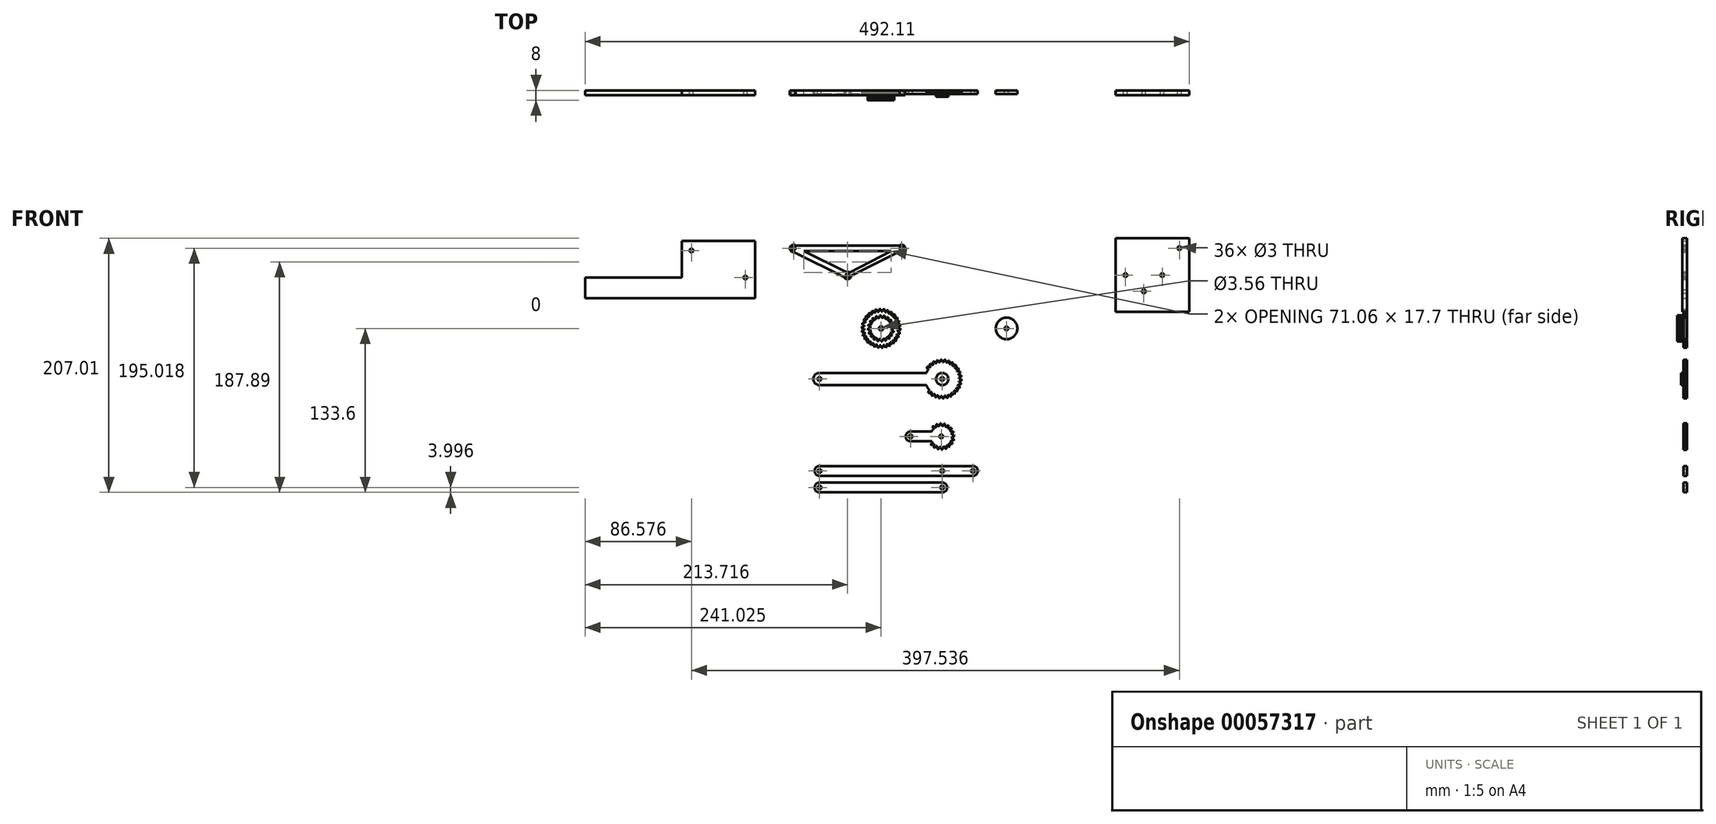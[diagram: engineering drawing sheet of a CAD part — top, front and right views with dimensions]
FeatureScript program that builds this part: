
annotation { "Feature Type Name" : "Feature", "Feature Type Description" : "" }
export const myFeature = defineFeature(function(context is Context, id is Id, definition is map)
    precondition{}
    {
        {
            var Q0;
            Q0=qCreatedBy(makeId("Front.planeOp"),FACE);
            var sketch = newSketch(context, id + "F0", { "sketchPlane" : qUnion([Q0])});
            skCircle(sketch, "E0", {"center": v(0, 0) * mm, "radius": 13.8 * mm});
            skCircle(sketch, "E1", {"center": v(0, 0) * mm, "radius": 15 * mm, "construction": true});
            skCircle(sketch, "E2", {"center": v(0, 0) * mm, "radius": 15.75 * mm, "construction": true});
            skLineSegment(sketch, "E3", {"start": v(0, 0) * mm, "end": v(0, 26.9) * mm, "construction": true});
            skCircle(sketch, "E4", {"center": v(0, 0) * mm, "radius": 14.1 * mm, "construction": true});
            skLineSegment(sketch, "E5", {"start": v(0, 0) * mm, "end": v(-1.5, 26.52) * mm, "construction": true});
            skLineSegment(sketch, "E6", {"start": v(0, 15) * mm, "end": v(-9, 15) * mm, "construction": true});
            skLineSegment(sketch, "E7", {"start": v(0, 15) * mm, "end": v(-16.93, 8.84) * mm, "construction": true});
            skCircle(sketch, "E8", {"center": v(0, 15) * mm, "radius": 2.5 * mm, "construction": true});
            skCircle(sketch, "E9", {"center": v(-2.25, 13.91) * mm, "radius": 2.5 * mm, "construction": true});
            skArc(sketch, "E10", {"start": v(-0.54, 15.74) * mm, "mid": v(0.06, 14.86) * mm, "end": v(0.25, 13.8) * mm});
            skArc(sketch, "E11.MirrorCS", {"start": v(-1.24, 15.7) * mm, "mid": v(-1.75, 14.75) * mm, "end": v(-1.8, 13.68) * mm});
            skLineSegment(sketch, "E12", {"start": v(-1.24, 15.7) * mm, "end": v(-0.54, 15.74) * mm});
            skArc(sketch, "E13.1.0", {"start": v(-4.48, 15.1) * mm, "mid": v(-4.77, 14.07) * mm, "end": v(-4.61, 13) * mm});
            skLineSegment(sketch, "E13.1.1", {"start": v(-4.48, 15.1) * mm, "end": v(-3.8, 15.28) * mm});
            skArc(sketch, "E13.1.2", {"start": v(-3.8, 15.28) * mm, "mid": v(-3.03, 14.54) * mm, "end": v(-2.63, 13.55) * mm});
            skArc(sketch, "E13.2.0", {"start": v(-7.52, 13.84) * mm, "mid": v(-7.6, 12.77) * mm, "end": v(-7.21, 11.76) * mm});
            skLineSegment(sketch, "E13.2.1", {"start": v(-7.52, 13.84) * mm, "end": v(-6.9, 14.16) * mm});
            skArc(sketch, "E13.2.2", {"start": v(-6.9, 14.16) * mm, "mid": v(-5.98, 13.6) * mm, "end": v(-5.39, 12.7) * mm});
            skArc(sketch, "E13.3.0", {"start": v(-10.23, 11.97) * mm, "mid": v(-10.08, 10.9) * mm, "end": v(-9.5, 10) * mm});
            skLineSegment(sketch, "E13.3.1", {"start": v(-10.23, 11.97) * mm, "end": v(-9.7, 12.41) * mm});
            skArc(sketch, "E13.3.2", {"start": v(-9.7, 12.41) * mm, "mid": v(-8.68, 12.06) * mm, "end": v(-7.91, 11.3) * mm});
            skArc(sketch, "E13.4.0", {"start": v(-12.5, 9.58) * mm, "mid": v(-12.13, 8.57) * mm, "end": v(-11.37, 7.81) * mm});
            skLineSegment(sketch, "E13.4.1", {"start": v(-12.5, 9.58) * mm, "end": v(-12.06, 10.13) * mm});
            skArc(sketch, "E13.4.2", {"start": v(-12.06, 10.13) * mm, "mid": v(-11, 9.99) * mm, "end": v(-10.09, 9.41) * mm});
            skArc(sketch, "E13.5.0", {"start": v(-14.22, 6.78) * mm, "mid": v(-13.65, 5.86) * mm, "end": v(-12.75, 5.28) * mm});
            skLineSegment(sketch, "E13.5.1", {"start": v(-14.22, 6.78) * mm, "end": v(-13.9, 7.4) * mm});
            skArc(sketch, "E13.5.2", {"start": v(-13.9, 7.4) * mm, "mid": v(-12.83, 7.48) * mm, "end": v(-11.82, 7.11) * mm});
            skArc(sketch, "E13.6.0", {"start": v(-15.32, 3.67) * mm, "mid": v(-14.57, 2.9) * mm, "end": v(-13.57, 2.51) * mm});
            skLineSegment(sketch, "E13.6.1", {"start": v(-15.32, 3.67) * mm, "end": v(-15.14, 4.35) * mm});
            skArc(sketch, "E13.6.2", {"start": v(-15.14, 4.35) * mm, "mid": v(-14.1, 4.65) * mm, "end": v(-13.04, 4.5) * mm});
            skArc(sketch, "E13.7.0", {"start": v(-15.74, 0.4) * mm, "mid": v(-14.85, -0.2) * mm, "end": v(-13.8, -0.37) * mm});
            skLineSegment(sketch, "E13.7.1", {"start": v(-15.74, 0.4) * mm, "end": v(-15.71, 1.1) * mm});
            skArc(sketch, "E13.7.2", {"start": v(-15.71, 1.1) * mm, "mid": v(-14.77, 1.62) * mm, "end": v(-13.7, 1.69) * mm});
            skArc(sketch, "E13.8.0", {"start": v(-15.49, -2.88) * mm, "mid": v(-14.49, -3.28) * mm, "end": v(-13.42, -3.23) * mm});
            skLineSegment(sketch, "E13.8.1", {"start": v(-15.49, -2.88) * mm, "end": v(-15.6, -2.19) * mm});
            skArc(sketch, "E13.8.2", {"start": v(-15.6, -2.19) * mm, "mid": v(-14.78, -1.49) * mm, "end": v(-13.75, -1.2) * mm});
            skArc(sketch, "E13.9.0", {"start": v(-14.55, -6.03) * mm, "mid": v(-13.5, -6.22) * mm, "end": v(-12.45, -5.94) * mm});
            skLineSegment(sketch, "E13.9.1", {"start": v(-14.55, -6.03) * mm, "end": v(-14.8, -5.38) * mm});
            skArc(sketch, "E13.9.2", {"start": v(-14.8, -5.38) * mm, "mid": v(-14.15, -4.53) * mm, "end": v(-13.2, -4.03) * mm});
            skArc(sketch, "E13.10.0", {"start": v(-12.98, -8.93) * mm, "mid": v(-11.9, -8.89) * mm, "end": v(-10.94, -8.4) * mm});
            skLineSegment(sketch, "E13.10.1", {"start": v(-12.98, -8.93) * mm, "end": v(-13.36, -8.34) * mm});
            skArc(sketch, "E13.10.2", {"start": v(-13.36, -8.34) * mm, "mid": v(-12.9, -7.37) * mm, "end": v(-12.07, -6.69) * mm});
            skArc(sketch, "E13.11.0", {"start": v(-10.84, -11.43) * mm, "mid": v(-9.8, -11.17) * mm, "end": v(-8.96, -10.5) * mm});
            skLineSegment(sketch, "E13.11.1", {"start": v(-10.84, -11.43) * mm, "end": v(-11.33, -10.94) * mm});
            skArc(sketch, "E13.11.2", {"start": v(-11.33, -10.94) * mm, "mid": v(-11.08, -9.9) * mm, "end": v(-10.42, -9.05) * mm});
            skArc(sketch, "E13.12.0", {"start": v(-8.23, -13.43) * mm, "mid": v(-7.26, -12.96) * mm, "end": v(-6.58, -12.13) * mm});
            skLineSegment(sketch, "E13.12.1", {"start": v(-8.23, -13.43) * mm, "end": v(-8.81, -13.05) * mm});
            skArc(sketch, "E13.12.2", {"start": v(-8.81, -13.05) * mm, "mid": v(-8.78, -11.98) * mm, "end": v(-8.3, -11.02) * mm});
            skArc(sketch, "E13.13.0", {"start": v(-5.25, -14.85) * mm, "mid": v(-4.4, -14.19) * mm, "end": v(-3.91, -13.23) * mm});
            skLineSegment(sketch, "E13.13.1", {"start": v(-5.25, -14.85) * mm, "end": v(-5.9, -14.6) * mm});
            skArc(sketch, "E13.13.2", {"start": v(-5.9, -14.6) * mm, "mid": v(-6.1, -13.54) * mm, "end": v(-5.84, -12.5) * mm});
            skArc(sketch, "E13.14.0", {"start": v(-2.05, -15.62) * mm, "mid": v(-1.36, -14.8) * mm, "end": v(-1.08, -13.76) * mm});
            skLineSegment(sketch, "E13.14.1", {"start": v(-2.05, -15.62) * mm, "end": v(-2.74, -15.5) * mm});
            skArc(sketch, "E13.14.2", {"start": v(-2.74, -15.5) * mm, "mid": v(-3.15, -14.52) * mm, "end": v(-3.1, -13.44) * mm});
            skArc(sketch, "E13.15.0", {"start": v(1.24, -15.7) * mm, "mid": v(1.75, -14.75) * mm, "end": v(1.8, -13.68) * mm});
            skLineSegment(sketch, "E13.15.1", {"start": v(1.24, -15.7) * mm, "end": v(0.54, -15.74) * mm});
            skArc(sketch, "E13.15.2", {"start": v(0.54, -15.74) * mm, "mid": v(-0.06, -14.86) * mm, "end": v(-0.25, -13.8) * mm});
            skArc(sketch, "E13.16.0", {"start": v(4.48, -15.1) * mm, "mid": v(4.77, -14.07) * mm, "end": v(4.61, -13) * mm});
            skLineSegment(sketch, "E13.16.1", {"start": v(4.48, -15.1) * mm, "end": v(3.8, -15.28) * mm});
            skArc(sketch, "E13.16.2", {"start": v(3.8, -15.28) * mm, "mid": v(3.03, -14.54) * mm, "end": v(2.63, -13.55) * mm});
            skArc(sketch, "E13.17.0", {"start": v(7.52, -13.84) * mm, "mid": v(7.6, -12.77) * mm, "end": v(7.21, -11.76) * mm});
            skLineSegment(sketch, "E13.17.1", {"start": v(7.52, -13.84) * mm, "end": v(6.9, -14.16) * mm});
            skArc(sketch, "E13.17.2", {"start": v(6.9, -14.16) * mm, "mid": v(5.98, -13.6) * mm, "end": v(5.39, -12.7) * mm});
            skArc(sketch, "E13.18.0", {"start": v(10.23, -11.97) * mm, "mid": v(10.08, -10.9) * mm, "end": v(9.5, -10) * mm});
            skLineSegment(sketch, "E13.18.1", {"start": v(10.23, -11.97) * mm, "end": v(9.7, -12.41) * mm});
            skArc(sketch, "E13.18.2", {"start": v(9.7, -12.41) * mm, "mid": v(8.68, -12.06) * mm, "end": v(7.91, -11.3) * mm});
            skArc(sketch, "E13.19.0", {"start": v(12.5, -9.58) * mm, "mid": v(12.13, -8.57) * mm, "end": v(11.37, -7.81) * mm});
            skLineSegment(sketch, "E13.19.1", {"start": v(12.5, -9.58) * mm, "end": v(12.06, -10.13) * mm});
            skArc(sketch, "E13.19.2", {"start": v(12.06, -10.13) * mm, "mid": v(11, -9.99) * mm, "end": v(10.09, -9.41) * mm});
            skArc(sketch, "E13.20.0", {"start": v(14.22, -6.78) * mm, "mid": v(13.65, -5.86) * mm, "end": v(12.75, -5.28) * mm});
            skLineSegment(sketch, "E13.20.1", {"start": v(14.22, -6.78) * mm, "end": v(13.9, -7.4) * mm});
            skArc(sketch, "E13.20.2", {"start": v(13.9, -7.4) * mm, "mid": v(12.83, -7.48) * mm, "end": v(11.82, -7.11) * mm});
            skArc(sketch, "E13.21.0", {"start": v(15.32, -3.67) * mm, "mid": v(14.57, -2.9) * mm, "end": v(13.57, -2.51) * mm});
            skLineSegment(sketch, "E13.21.1", {"start": v(15.32, -3.67) * mm, "end": v(15.14, -4.35) * mm});
            skArc(sketch, "E13.21.2", {"start": v(15.14, -4.35) * mm, "mid": v(14.1, -4.65) * mm, "end": v(13.04, -4.5) * mm});
            skArc(sketch, "E13.22.0", {"start": v(15.74, -0.4) * mm, "mid": v(14.85, 0.2) * mm, "end": v(13.8, 0.37) * mm});
            skLineSegment(sketch, "E13.22.1", {"start": v(15.74, -0.4) * mm, "end": v(15.71, -1.1) * mm});
            skArc(sketch, "E13.22.2", {"start": v(15.71, -1.1) * mm, "mid": v(14.77, -1.62) * mm, "end": v(13.7, -1.69) * mm});
            skArc(sketch, "E13.23.0", {"start": v(15.49, 2.88) * mm, "mid": v(14.49, 3.28) * mm, "end": v(13.42, 3.23) * mm});
            skLineSegment(sketch, "E13.23.1", {"start": v(15.49, 2.88) * mm, "end": v(15.6, 2.19) * mm});
            skArc(sketch, "E13.23.2", {"start": v(15.6, 2.19) * mm, "mid": v(14.78, 1.49) * mm, "end": v(13.75, 1.2) * mm});
            skArc(sketch, "E13.24.0", {"start": v(14.55, 6.03) * mm, "mid": v(13.5, 6.22) * mm, "end": v(12.45, 5.94) * mm});
            skLineSegment(sketch, "E13.24.1", {"start": v(14.55, 6.03) * mm, "end": v(14.8, 5.38) * mm});
            skArc(sketch, "E13.24.2", {"start": v(14.8, 5.38) * mm, "mid": v(14.15, 4.53) * mm, "end": v(13.2, 4.03) * mm});
            skArc(sketch, "E13.25.0", {"start": v(12.98, 8.93) * mm, "mid": v(11.9, 8.89) * mm, "end": v(10.94, 8.4) * mm});
            skLineSegment(sketch, "E13.25.1", {"start": v(12.98, 8.93) * mm, "end": v(13.36, 8.34) * mm});
            skArc(sketch, "E13.25.2", {"start": v(13.36, 8.34) * mm, "mid": v(12.9, 7.37) * mm, "end": v(12.07, 6.69) * mm});
            skArc(sketch, "E13.26.0", {"start": v(10.84, 11.43) * mm, "mid": v(9.8, 11.17) * mm, "end": v(8.96, 10.5) * mm});
            skLineSegment(sketch, "E13.26.1", {"start": v(10.84, 11.43) * mm, "end": v(11.33, 10.94) * mm});
            skArc(sketch, "E13.26.2", {"start": v(11.33, 10.94) * mm, "mid": v(11.08, 9.9) * mm, "end": v(10.42, 9.05) * mm});
            skArc(sketch, "E13.27.0", {"start": v(8.23, 13.43) * mm, "mid": v(7.26, 12.96) * mm, "end": v(6.58, 12.13) * mm});
            skLineSegment(sketch, "E13.27.1", {"start": v(8.23, 13.43) * mm, "end": v(8.81, 13.05) * mm});
            skArc(sketch, "E13.27.2", {"start": v(8.81, 13.05) * mm, "mid": v(8.78, 11.98) * mm, "end": v(8.3, 11.02) * mm});
            skArc(sketch, "E13.28.0", {"start": v(5.25, 14.85) * mm, "mid": v(4.4, 14.19) * mm, "end": v(3.91, 13.23) * mm});
            skLineSegment(sketch, "E13.28.1", {"start": v(5.25, 14.85) * mm, "end": v(5.9, 14.6) * mm});
            skArc(sketch, "E13.28.2", {"start": v(5.9, 14.6) * mm, "mid": v(6.1, 13.54) * mm, "end": v(5.84, 12.5) * mm});
            skArc(sketch, "E13.29.0", {"start": v(2.05, 15.62) * mm, "mid": v(1.36, 14.8) * mm, "end": v(1.08, 13.76) * mm});
            skLineSegment(sketch, "E13.29.1", {"start": v(2.05, 15.62) * mm, "end": v(2.74, 15.5) * mm});
            skArc(sketch, "E13.29.2", {"start": v(2.74, 15.5) * mm, "mid": v(3.15, 14.52) * mm, "end": v(3.1, 13.44) * mm});
            skCircle(sketch, "E14", {"center": v(0, 0) * mm, "radius": 1.5 * mm});
            skLineSegment(sketch, "E15", {"start": v(0, 0) * mm, "end": v(61.86, 0) * mm, "construction": true});
            skCircle(sketch, "E16", {"center": v(51.4, 0) * mm, "radius": 1.5 * mm});
            skCircle(sketch, "E17", {"center": v(51.4, 0) * mm, "radius": 8.8 * mm});
            skCircle(sketch, "E18", {"center": v(51.4, 0) * mm, "radius": 10 * mm, "construction": true});
            skCircle(sketch, "E19", {"center": v(51.4, 0) * mm, "radius": 10.75 * mm, "construction": true});
            skLineSegment(sketch, "E20", {"start": v(51.4, 0) * mm, "end": v(51.4, 18.55) * mm, "construction": true});
            skLineSegment(sketch, "E21", {"start": v(51.4, 0) * mm, "end": v(50.35, 18.55) * mm, "construction": true});
            skLineSegment(sketch, "E22", {"start": v(51.4, 10) * mm, "end": v(34.59, 10) * mm, "construction": true});
            skLineSegment(sketch, "E23", {"start": v(51.4, 10) * mm, "end": v(35.17, 4.1) * mm, "construction": true});
            skCircle(sketch, "E24", {"center": v(51.4, 0) * mm, "radius": 9.4 * mm, "construction": true});
            skCircle(sketch, "E25", {"center": v(51.4, 10) * mm, "radius": 2.5 * mm, "construction": true});
            skCircle(sketch, "E26", {"center": v(49.07, 9.1) * mm, "radius": 2.5 * mm, "construction": true});
            skArc(sketch, "E27", {"start": v(50.96, 10.74) * mm, "mid": v(51.46, 9.83) * mm, "end": v(51.55, 8.8) * mm});
            skArc(sketch, "E28.MirrorCS", {"start": v(50.63, 10.72) * mm, "mid": v(50.23, 9.76) * mm, "end": v(50.26, 8.72) * mm});
            skLineSegment(sketch, "E29", {"start": v(50.63, 10.72) * mm, "end": v(50.96, 10.74) * mm});
            skArc(sketch, "E30.1.0", {"start": v(47.66, 10.08) * mm, "mid": v(48.42, 9.37) * mm, "end": v(48.82, 8.41) * mm});
            skLineSegment(sketch, "E30.1.1", {"start": v(47.35, 9.96) * mm, "end": v(47.66, 10.08) * mm});
            skArc(sketch, "E30.1.2", {"start": v(47.35, 9.96) * mm, "mid": v(47.27, 8.92) * mm, "end": v(47.62, 7.94) * mm});
            skArc(sketch, "E30.2.0", {"start": v(44.73, 8.43) * mm, "mid": v(45.67, 7.99) * mm, "end": v(46.35, 7.2) * mm});
            skLineSegment(sketch, "E30.2.1", {"start": v(44.47, 8.22) * mm, "end": v(44.73, 8.43) * mm});
            skArc(sketch, "E30.2.2", {"start": v(44.47, 8.22) * mm, "mid": v(44.72, 7.2) * mm, "end": v(45.35, 6.39) * mm});
            skArc(sketch, "E30.3.0", {"start": v(42.45, 5.95) * mm, "mid": v(43.48, 5.83) * mm, "end": v(44.37, 5.3) * mm});
            skLineSegment(sketch, "E30.3.1", {"start": v(42.27, 5.68) * mm, "end": v(42.45, 5.95) * mm});
            skArc(sketch, "E30.3.2", {"start": v(42.27, 5.68) * mm, "mid": v(42.82, 4.8) * mm, "end": v(43.67, 4.2) * mm});
            skArc(sketch, "E30.4.0", {"start": v(41.05, 2.9) * mm, "mid": v(42.07, 3.1) * mm, "end": v(43.08, 2.86) * mm});
            skLineSegment(sketch, "E30.4.1", {"start": v(40.96, 2.58) * mm, "end": v(41.05, 2.9) * mm});
            skArc(sketch, "E30.4.2", {"start": v(40.96, 2.58) * mm, "mid": v(41.75, 1.9) * mm, "end": v(42.75, 1.6) * mm});
            skArc(sketch, "E30.5.0", {"start": v(40.66, -0.44) * mm, "mid": v(41.57, 0.06) * mm, "end": v(42.6, 0.15) * mm});
            skLineSegment(sketch, "E30.5.1", {"start": v(40.68, -0.77) * mm, "end": v(40.66, -0.44) * mm});
            skArc(sketch, "E30.5.2", {"start": v(40.68, -0.77) * mm, "mid": v(41.64, -1.17) * mm, "end": v(42.68, -1.14) * mm});
            skArc(sketch, "E30.6.0", {"start": v(41.32, -3.74) * mm, "mid": v(42.03, -2.98) * mm, "end": v(42.99, -2.58) * mm});
            skLineSegment(sketch, "E30.6.1", {"start": v(41.44, -4.05) * mm, "end": v(41.32, -3.74) * mm});
            skArc(sketch, "E30.6.2", {"start": v(41.44, -4.05) * mm, "mid": v(42.48, -4.13) * mm, "end": v(43.46, -3.78) * mm});
            skArc(sketch, "E30.7.0", {"start": v(42.97, -6.67) * mm, "mid": v(43.41, -5.73) * mm, "end": v(44.2, -5.05) * mm});
            skLineSegment(sketch, "E30.7.1", {"start": v(43.18, -6.93) * mm, "end": v(42.97, -6.67) * mm});
            skArc(sketch, "E30.7.2", {"start": v(43.18, -6.93) * mm, "mid": v(44.2, -6.68) * mm, "end": v(45.01, -6.05) * mm});
            skArc(sketch, "E30.8.0", {"start": v(45.45, -8.95) * mm, "mid": v(45.57, -7.92) * mm, "end": v(46.11, -7.03) * mm});
            skLineSegment(sketch, "E30.8.1", {"start": v(45.72, -9.13) * mm, "end": v(45.45, -8.95) * mm});
            skArc(sketch, "E30.8.2", {"start": v(45.72, -9.13) * mm, "mid": v(46.6, -8.59) * mm, "end": v(47.2, -7.73) * mm});
            skArc(sketch, "E30.9.0", {"start": v(48.5, -10.35) * mm, "mid": v(48.3, -9.33) * mm, "end": v(48.54, -8.32) * mm});
            skLineSegment(sketch, "E30.9.1", {"start": v(48.82, -10.44) * mm, "end": v(48.5, -10.35) * mm});
            skArc(sketch, "E30.9.2", {"start": v(48.82, -10.44) * mm, "mid": v(49.5, -9.65) * mm, "end": v(49.8, -8.65) * mm});
            skArc(sketch, "E30.10.0", {"start": v(51.85, -10.74) * mm, "mid": v(51.34, -9.83) * mm, "end": v(51.25, -8.8) * mm});
            skLineSegment(sketch, "E30.10.1", {"start": v(52.17, -10.72) * mm, "end": v(51.85, -10.74) * mm});
            skArc(sketch, "E30.10.2", {"start": v(52.17, -10.72) * mm, "mid": v(52.57, -9.76) * mm, "end": v(52.54, -8.72) * mm});
            skArc(sketch, "E30.11.0", {"start": v(55.14, -10.08) * mm, "mid": v(54.38, -9.37) * mm, "end": v(53.98, -8.41) * mm});
            skLineSegment(sketch, "E30.11.1", {"start": v(55.45, -9.96) * mm, "end": v(55.14, -10.08) * mm});
            skArc(sketch, "E30.11.2", {"start": v(55.45, -9.96) * mm, "mid": v(55.53, -8.92) * mm, "end": v(55.18, -7.94) * mm});
            skArc(sketch, "E30.12.0", {"start": v(58.07, -8.43) * mm, "mid": v(57.13, -7.99) * mm, "end": v(56.45, -7.2) * mm});
            skLineSegment(sketch, "E30.12.1", {"start": v(58.33, -8.22) * mm, "end": v(58.07, -8.43) * mm});
            skArc(sketch, "E30.12.2", {"start": v(58.33, -8.22) * mm, "mid": v(58.09, -7.2) * mm, "end": v(57.45, -6.39) * mm});
            skArc(sketch, "E30.13.0", {"start": v(60.35, -5.95) * mm, "mid": v(59.32, -5.83) * mm, "end": v(58.43, -5.3) * mm});
            skLineSegment(sketch, "E30.13.1", {"start": v(60.53, -5.68) * mm, "end": v(60.35, -5.95) * mm});
            skArc(sketch, "E30.13.2", {"start": v(60.53, -5.68) * mm, "mid": v(59.99, -4.8) * mm, "end": v(59.13, -4.2) * mm});
            skArc(sketch, "E30.14.0", {"start": v(61.75, -2.9) * mm, "mid": v(60.73, -3.1) * mm, "end": v(59.72, -2.86) * mm});
            skLineSegment(sketch, "E30.14.1", {"start": v(61.84, -2.58) * mm, "end": v(61.75, -2.9) * mm});
            skArc(sketch, "E30.14.2", {"start": v(61.84, -2.58) * mm, "mid": v(61.05, -1.9) * mm, "end": v(60.05, -1.6) * mm});
            skArc(sketch, "E30.15.0", {"start": v(62.14, 0.44) * mm, "mid": v(61.23, -0.06) * mm, "end": v(60.2, -0.15) * mm});
            skLineSegment(sketch, "E30.15.1", {"start": v(62.12, 0.77) * mm, "end": v(62.14, 0.44) * mm});
            skArc(sketch, "E30.15.2", {"start": v(62.12, 0.77) * mm, "mid": v(61.16, 1.17) * mm, "end": v(60.12, 1.14) * mm});
            skArc(sketch, "E30.16.0", {"start": v(61.48, 3.74) * mm, "mid": v(60.77, 2.98) * mm, "end": v(59.81, 2.58) * mm});
            skLineSegment(sketch, "E30.16.1", {"start": v(61.36, 4.05) * mm, "end": v(61.48, 3.74) * mm});
            skArc(sketch, "E30.16.2", {"start": v(61.36, 4.05) * mm, "mid": v(60.32, 4.13) * mm, "end": v(59.34, 3.78) * mm});
            skArc(sketch, "E30.17.0", {"start": v(59.83, 6.67) * mm, "mid": v(59.39, 5.73) * mm, "end": v(58.6, 5.05) * mm});
            skLineSegment(sketch, "E30.17.1", {"start": v(59.62, 6.93) * mm, "end": v(59.83, 6.67) * mm});
            skArc(sketch, "E30.17.2", {"start": v(59.62, 6.93) * mm, "mid": v(58.61, 6.68) * mm, "end": v(57.79, 6.05) * mm});
            skArc(sketch, "E30.18.0", {"start": v(57.35, 8.95) * mm, "mid": v(57.23, 7.92) * mm, "end": v(56.7, 7.03) * mm});
            skLineSegment(sketch, "E30.18.1", {"start": v(57.08, 9.13) * mm, "end": v(57.35, 8.95) * mm});
            skArc(sketch, "E30.18.2", {"start": v(57.08, 9.13) * mm, "mid": v(56.2, 8.59) * mm, "end": v(55.6, 7.73) * mm});
            skArc(sketch, "E30.19.0", {"start": v(54.3, 10.35) * mm, "mid": v(54.5, 9.33) * mm, "end": v(54.26, 8.32) * mm});
            skLineSegment(sketch, "E30.19.1", {"start": v(53.98, 10.44) * mm, "end": v(54.3, 10.35) * mm});
            skArc(sketch, "E30.19.2", {"start": v(53.98, 10.44) * mm, "mid": v(53.3, 9.65) * mm, "end": v(53, 8.65) * mm});
            skCircle(sketch, "E31", {"center": v(-50.82, 0) * mm, "radius": 1.78 * mm});
            skCircle(sketch, "E32", {"center": v(-50.82, 0) * mm, "radius": 14.1 * mm, "construction": true});
            skCircle(sketch, "E33", {"center": v(-50.82, 0) * mm, "radius": 15 * mm, "construction": true});
            skCircle(sketch, "E34", {"center": v(-50.82, 0) * mm, "radius": 15.75 * mm, "construction": true});
            skArc(sketch, "E35", {"start": v(-60.24, 10.09) * mm, "mid": v(-60.62, 9.71) * mm, "end": v(-61, 9.33) * mm});
            skArc(sketch, "E36", {"start": v(-54.59, 7.95) * mm, "mid": v(-54.88, 7.8) * mm, "end": v(-55.18, 7.65) * mm});
            skCircle(sketch, "E37", {"center": v(-50.82, 0) * mm, "radius": 9.4 * mm, "construction": true});
            skCircle(sketch, "E38", {"center": v(-50.82, 0) * mm, "radius": 10 * mm, "construction": true});
            skCircle(sketch, "E39", {"center": v(-50.82, 0) * mm, "radius": 10.75 * mm, "construction": true});
            skLineSegment(sketch, "E40", {"start": v(-50.82, 0) * mm, "end": v(-50.82, 24.13) * mm, "construction": true});
            skLineSegment(sketch, "E41", {"start": v(-50.82, 0) * mm, "end": v(-52.2, 24.2) * mm, "construction": true});
            skLineSegment(sketch, "E42", {"start": v(-50.82, 15) * mm, "end": v(-70.83, 15) * mm, "construction": true});
            skLineSegment(sketch, "E43", {"start": v(-50.82, 15) * mm, "end": v(-70.68, 7.77) * mm, "construction": true});
            skLineSegment(sketch, "E44", {"start": v(-50.82, 10) * mm, "end": v(-70.83, 10) * mm, "construction": true});
            skLineSegment(sketch, "E45", {"start": v(-50.82, 10) * mm, "end": v(-70.68, 2.77) * mm, "construction": true});
            skCircle(sketch, "E46", {"center": v(-50.82, 15) * mm, "radius": 2.5 * mm, "construction": true});
            skCircle(sketch, "E47", {"center": v(-50.82, 10) * mm, "radius": 2.5 * mm, "construction": true});
            skCircle(sketch, "E48", {"center": v(-53.17, 14.14) * mm, "radius": 2.5 * mm, "construction": true});
            skCircle(sketch, "E49", {"center": v(-53.17, 9.14) * mm, "radius": 2.5 * mm, "construction": true});
            skArc(sketch, "E50", {"start": v(-51.25, 15.74) * mm, "mid": v(-50.77, 14.83) * mm, "end": v(-50.7, 13.8) * mm});
            skArc(sketch, "E51", {"start": v(-51.25, 10.74) * mm, "mid": v(-50.77, 9.83) * mm, "end": v(-50.7, 8.8) * mm});
            skArc(sketch, "E52.MirrorCS", {"start": v(-52.18, 15.7) * mm, "mid": v(-52.56, 14.73) * mm, "end": v(-52.51, 13.7) * mm});
            skArc(sketch, "E53.MirrorCS", {"start": v(-51.62, 10.72) * mm, "mid": v(-52, 9.76) * mm, "end": v(-51.95, 8.73) * mm});
            skLineSegment(sketch, "E54", {"start": v(-52.18, 15.7) * mm, "end": v(-51.25, 15.74) * mm});
            skLineSegment(sketch, "E55", {"start": v(-51.62, 10.72) * mm, "end": v(-51.25, 10.74) * mm});
            skArc(sketch, "E56.1.0", {"start": v(-55.42, 15.07) * mm, "mid": v(-55.58, 14.05) * mm, "end": v(-55.32, 13.04) * mm});
            skLineSegment(sketch, "E56.1.1", {"start": v(-55.42, 15.07) * mm, "end": v(-54.52, 15.31) * mm});
            skArc(sketch, "E56.1.2", {"start": v(-54.52, 15.31) * mm, "mid": v(-53.85, 14.52) * mm, "end": v(-53.57, 13.52) * mm});
            skArc(sketch, "E56.2.0", {"start": v(-58.45, 13.78) * mm, "mid": v(-58.4, 12.75) * mm, "end": v(-57.94, 11.82) * mm});
            skLineSegment(sketch, "E56.2.1", {"start": v(-58.45, 13.78) * mm, "end": v(-57.62, 14.2) * mm});
            skArc(sketch, "E56.2.2", {"start": v(-57.62, 14.2) * mm, "mid": v(-56.8, 13.57) * mm, "end": v(-56.32, 12.66) * mm});
            skArc(sketch, "E56.3.0", {"start": v(-61.15, 11.9) * mm, "mid": v(-60.88, 10.9) * mm, "end": v(-60.24, 10.09) * mm});
            skLineSegment(sketch, "E56.3.1", {"start": v(-61.15, 11.9) * mm, "end": v(-60.43, 12.49) * mm});
            skArc(sketch, "E56.3.2", {"start": v(-60.43, 12.49) * mm, "mid": v(-59.5, 12.03) * mm, "end": v(-58.83, 11.24) * mm});
            skArc(sketch, "E56.4.0", {"start": v(-63.4, 9.5) * mm, "mid": v(-62.93, 8.57) * mm, "end": v(-62.13, 7.9) * mm});
            skLineSegment(sketch, "E56.4.1", {"start": v(-63.4, 9.5) * mm, "end": v(-62.81, 10.22) * mm});
            skArc(sketch, "E56.4.2", {"start": v(-62.81, 10.22) * mm, "mid": v(-61.8, 9.96) * mm, "end": v(-61, 9.33) * mm});
            skArc(sketch, "E56.5.0", {"start": v(-65.1, 6.67) * mm, "mid": v(-64.45, 5.86) * mm, "end": v(-63.53, 5.39) * mm});
            skLineSegment(sketch, "E56.5.1", {"start": v(-65.1, 6.67) * mm, "end": v(-64.67, 7.5) * mm});
            skArc(sketch, "E56.5.2", {"start": v(-64.67, 7.5) * mm, "mid": v(-63.64, 7.46) * mm, "end": v(-62.71, 7) * mm});
            skArc(sketch, "E56.6.0", {"start": v(-66.17, 3.56) * mm, "mid": v(-65.37, 2.9) * mm, "end": v(-64.37, 2.63) * mm});
            skLineSegment(sketch, "E56.6.1", {"start": v(-66.17, 3.56) * mm, "end": v(-65.93, 4.46) * mm});
            skArc(sketch, "E56.6.2", {"start": v(-65.93, 4.46) * mm, "mid": v(-64.91, 4.64) * mm, "end": v(-63.9, 4.38) * mm});
            skArc(sketch, "E56.7.0", {"start": v(-66.57, 0.3) * mm, "mid": v(-65.65, -0.18) * mm, "end": v(-64.62, -0.25) * mm});
            skLineSegment(sketch, "E56.7.1", {"start": v(-66.57, 0.3) * mm, "end": v(-66.53, 1.22) * mm});
            skArc(sketch, "E56.7.2", {"start": v(-66.53, 1.22) * mm, "mid": v(-65.57, 1.6) * mm, "end": v(-64.53, 1.57) * mm});
            skArc(sketch, "E56.8.0", {"start": v(-66.29, -3) * mm, "mid": v(-65.3, -3.26) * mm, "end": v(-64.27, -3.1) * mm});
            skLineSegment(sketch, "E56.8.1", {"start": v(-66.29, -3) * mm, "end": v(-66.44, -2.07) * mm});
            skArc(sketch, "E56.8.2", {"start": v(-66.44, -2.07) * mm, "mid": v(-65.58, -1.5) * mm, "end": v(-64.56, -1.32) * mm});
            skArc(sketch, "E56.9.0", {"start": v(-65.33, -6.14) * mm, "mid": v(-64.3, -6.2) * mm, "end": v(-63.33, -5.84) * mm});
            skLineSegment(sketch, "E56.9.1", {"start": v(-65.33, -6.14) * mm, "end": v(-65.67, -5.27) * mm});
            skArc(sketch, "E56.9.2", {"start": v(-65.67, -5.27) * mm, "mid": v(-64.95, -4.53) * mm, "end": v(-63.99, -4.14) * mm});
            skArc(sketch, "E56.10.0", {"start": v(-63.74, -9.02) * mm, "mid": v(-62.71, -8.87) * mm, "end": v(-61.84, -8.3) * mm});
            skLineSegment(sketch, "E56.10.1", {"start": v(-63.74, -9.02) * mm, "end": v(-64.25, -8.24) * mm});
            skArc(sketch, "E56.10.2", {"start": v(-64.25, -8.24) * mm, "mid": v(-63.7, -7.37) * mm, "end": v(-62.84, -6.79) * mm});
            skArc(sketch, "E56.11.0", {"start": v(-61.58, -11.5) * mm, "mid": v(-60.6, -11.14) * mm, "end": v(-59.87, -10.42) * mm});
            skLineSegment(sketch, "E56.11.1", {"start": v(-61.58, -11.5) * mm, "end": v(-62.24, -10.85) * mm});
            skArc(sketch, "E56.11.2", {"start": v(-62.24, -10.85) * mm, "mid": v(-61.88, -9.88) * mm, "end": v(-61.16, -9.14) * mm});
            skArc(sketch, "E56.12.0", {"start": v(-58.95, -13.5) * mm, "mid": v(-58.08, -12.93) * mm, "end": v(-57.5, -12.07) * mm});
            skLineSegment(sketch, "E56.12.1", {"start": v(-58.95, -13.5) * mm, "end": v(-59.73, -12.99) * mm});
            skArc(sketch, "E56.12.2", {"start": v(-59.73, -12.99) * mm, "mid": v(-59.59, -11.96) * mm, "end": v(-59.04, -11.09) * mm});
            skArc(sketch, "E56.13.0", {"start": v(-55.97, -14.89) * mm, "mid": v(-55.23, -14.16) * mm, "end": v(-54.85, -13.2) * mm});
            skLineSegment(sketch, "E56.13.1", {"start": v(-55.97, -14.89) * mm, "end": v(-56.84, -14.56) * mm});
            skArc(sketch, "E56.13.2", {"start": v(-56.84, -14.56) * mm, "mid": v(-56.9, -13.52) * mm, "end": v(-56.55, -12.55) * mm});
            skArc(sketch, "E56.14.0", {"start": v(-52.76, -15.63) * mm, "mid": v(-52.2, -14.77) * mm, "end": v(-52.02, -13.75) * mm});
            skLineSegment(sketch, "E56.14.1", {"start": v(-52.76, -15.63) * mm, "end": v(-53.68, -15.49) * mm});
            skArc(sketch, "E56.14.2", {"start": v(-53.68, -15.49) * mm, "mid": v(-53.96, -14.5) * mm, "end": v(-53.82, -13.47) * mm});
            skArc(sketch, "E56.15.0", {"start": v(-49.47, -15.7) * mm, "mid": v(-49.1, -14.73) * mm, "end": v(-49.14, -13.7) * mm});
            skLineSegment(sketch, "E56.15.1", {"start": v(-49.47, -15.7) * mm, "end": v(-50.4, -15.74) * mm});
            skArc(sketch, "E56.15.2", {"start": v(-50.4, -15.74) * mm, "mid": v(-50.88, -14.83) * mm, "end": v(-50.95, -13.8) * mm});
            skArc(sketch, "E56.16.0", {"start": v(-46.23, -15.07) * mm, "mid": v(-46.07, -14.05) * mm, "end": v(-46.33, -13.04) * mm});
            skLineSegment(sketch, "E56.16.1", {"start": v(-46.23, -15.07) * mm, "end": v(-47.13, -15.31) * mm});
            skArc(sketch, "E56.16.2", {"start": v(-47.13, -15.31) * mm, "mid": v(-47.8, -14.52) * mm, "end": v(-48.08, -13.52) * mm});
            skArc(sketch, "E56.17.0", {"start": v(-43.2, -13.78) * mm, "mid": v(-43.25, -12.75) * mm, "end": v(-43.71, -11.82) * mm});
            skLineSegment(sketch, "E56.17.1", {"start": v(-43.2, -13.78) * mm, "end": v(-44.03, -14.2) * mm});
            skArc(sketch, "E56.17.2", {"start": v(-44.03, -14.2) * mm, "mid": v(-44.84, -13.57) * mm, "end": v(-45.33, -12.66) * mm});
            skArc(sketch, "E56.18.0", {"start": v(-40.5, -11.9) * mm, "mid": v(-40.77, -10.9) * mm, "end": v(-41.41, -10.09) * mm});
            skLineSegment(sketch, "E56.18.1", {"start": v(-40.5, -11.9) * mm, "end": v(-41.22, -12.49) * mm});
            skArc(sketch, "E56.18.2", {"start": v(-41.22, -12.49) * mm, "mid": v(-42.15, -12.03) * mm, "end": v(-42.82, -11.24) * mm});
            skArc(sketch, "E56.19.0", {"start": v(-38.26, -9.5) * mm, "mid": v(-38.72, -8.57) * mm, "end": v(-39.52, -7.9) * mm});
            skLineSegment(sketch, "E56.19.1", {"start": v(-38.26, -9.5) * mm, "end": v(-38.84, -10.22) * mm});
            skArc(sketch, "E56.19.2", {"start": v(-38.84, -10.22) * mm, "mid": v(-39.84, -9.96) * mm, "end": v(-40.66, -9.33) * mm});
            skArc(sketch, "E56.20.0", {"start": v(-36.56, -6.67) * mm, "mid": v(-37.2, -5.86) * mm, "end": v(-38.12, -5.39) * mm});
            skLineSegment(sketch, "E56.20.1", {"start": v(-36.56, -6.67) * mm, "end": v(-36.98, -7.5) * mm});
            skArc(sketch, "E56.20.2", {"start": v(-36.98, -7.5) * mm, "mid": v(-38, -7.46) * mm, "end": v(-38.94, -7) * mm});
            skArc(sketch, "E56.21.0", {"start": v(-35.48, -3.56) * mm, "mid": v(-36.28, -2.9) * mm, "end": v(-37.28, -2.63) * mm});
            skLineSegment(sketch, "E56.21.1", {"start": v(-35.48, -3.56) * mm, "end": v(-35.72, -4.46) * mm});
            skArc(sketch, "E56.21.2", {"start": v(-35.72, -4.46) * mm, "mid": v(-36.74, -4.64) * mm, "end": v(-37.74, -4.38) * mm});
            skArc(sketch, "E56.22.0", {"start": v(-35.08, -0.3) * mm, "mid": v(-36, 0.18) * mm, "end": v(-37.03, 0.25) * mm});
            skLineSegment(sketch, "E56.22.1", {"start": v(-35.08, -0.3) * mm, "end": v(-35.12, -1.22) * mm});
            skArc(sketch, "E56.22.2", {"start": v(-35.12, -1.22) * mm, "mid": v(-36.08, -1.6) * mm, "end": v(-37.12, -1.57) * mm});
            skArc(sketch, "E56.23.0", {"start": v(-35.36, 3) * mm, "mid": v(-36.36, 3.26) * mm, "end": v(-37.38, 3.1) * mm});
            skLineSegment(sketch, "E56.23.1", {"start": v(-35.36, 3) * mm, "end": v(-35.21, 2.07) * mm});
            skArc(sketch, "E56.23.2", {"start": v(-35.21, 2.07) * mm, "mid": v(-36.07, 1.5) * mm, "end": v(-37.09, 1.32) * mm});
            skArc(sketch, "E56.24.0", {"start": v(-36.32, 6.14) * mm, "mid": v(-37.35, 6.2) * mm, "end": v(-38.32, 5.84) * mm});
            skLineSegment(sketch, "E56.24.1", {"start": v(-36.32, 6.14) * mm, "end": v(-35.98, 5.27) * mm});
            skArc(sketch, "E56.24.2", {"start": v(-35.98, 5.27) * mm, "mid": v(-36.7, 4.53) * mm, "end": v(-37.66, 4.14) * mm});
            skArc(sketch, "E56.25.0", {"start": v(-37.91, 9.02) * mm, "mid": v(-38.94, 8.87) * mm, "end": v(-39.8, 8.3) * mm});
            skLineSegment(sketch, "E56.25.1", {"start": v(-37.91, 9.02) * mm, "end": v(-37.4, 8.24) * mm});
            skArc(sketch, "E56.25.2", {"start": v(-37.4, 8.24) * mm, "mid": v(-37.95, 7.37) * mm, "end": v(-38.81, 6.79) * mm});
            skArc(sketch, "E56.26.0", {"start": v(-40.07, 11.5) * mm, "mid": v(-41.04, 11.14) * mm, "end": v(-41.78, 10.42) * mm});
            skLineSegment(sketch, "E56.26.1", {"start": v(-40.07, 11.5) * mm, "end": v(-39.41, 10.85) * mm});
            skArc(sketch, "E56.26.2", {"start": v(-39.41, 10.85) * mm, "mid": v(-39.77, 9.88) * mm, "end": v(-40.49, 9.14) * mm});
            skArc(sketch, "E56.27.0", {"start": v(-42.7, 13.5) * mm, "mid": v(-43.57, 12.93) * mm, "end": v(-44.14, 12.07) * mm});
            skLineSegment(sketch, "E56.27.1", {"start": v(-42.7, 13.5) * mm, "end": v(-41.92, 12.99) * mm});
            skArc(sketch, "E56.27.2", {"start": v(-41.92, 12.99) * mm, "mid": v(-42.06, 11.96) * mm, "end": v(-42.61, 11.09) * mm});
            skArc(sketch, "E56.28.0", {"start": v(-45.68, 14.89) * mm, "mid": v(-46.42, 14.16) * mm, "end": v(-46.8, 13.2) * mm});
            skLineSegment(sketch, "E56.28.1", {"start": v(-45.68, 14.89) * mm, "end": v(-44.81, 14.56) * mm});
            skArc(sketch, "E56.28.2", {"start": v(-44.81, 14.56) * mm, "mid": v(-44.74, 13.52) * mm, "end": v(-45.1, 12.55) * mm});
            skArc(sketch, "E56.29.0", {"start": v(-48.9, 15.63) * mm, "mid": v(-49.46, 14.77) * mm, "end": v(-49.63, 13.75) * mm});
            skLineSegment(sketch, "E56.29.1", {"start": v(-48.9, 15.63) * mm, "end": v(-47.97, 15.49) * mm});
            skArc(sketch, "E56.29.2", {"start": v(-47.97, 15.49) * mm, "mid": v(-47.69, 14.5) * mm, "end": v(-47.83, 13.47) * mm});
            skArc(sketch, "E57.1.0", {"start": v(-54.9, 9.95) * mm, "mid": v(-54.95, 8.92) * mm, "end": v(-54.59, 7.95) * mm});
            skArc(sketch, "E57.1.1", {"start": v(-54.55, 10.08) * mm, "mid": v(-53.8, 9.36) * mm, "end": v(-53.42, 8.4) * mm});
            skLineSegment(sketch, "E57.1.2", {"start": v(-54.9, 9.95) * mm, "end": v(-54.55, 10.08) * mm});
            skArc(sketch, "E57.2.0", {"start": v(-57.77, 8.2) * mm, "mid": v(-57.5, 7.2) * mm, "end": v(-56.86, 6.4) * mm});
            skArc(sketch, "E57.2.1", {"start": v(-57.48, 8.44) * mm, "mid": v(-56.56, 7.98) * mm, "end": v(-55.9, 7.2) * mm});
            skLineSegment(sketch, "E57.2.2", {"start": v(-57.77, 8.2) * mm, "end": v(-57.48, 8.44) * mm});
            skArc(sketch, "E57.3.0", {"start": v(-59.96, 5.66) * mm, "mid": v(-59.4, 4.8) * mm, "end": v(-58.54, 4.22) * mm});
            skArc(sketch, "E57.3.1", {"start": v(-59.77, 5.97) * mm, "mid": v(-58.74, 5.82) * mm, "end": v(-57.87, 5.27) * mm});
            skLineSegment(sketch, "E57.3.2", {"start": v(-59.96, 5.66) * mm, "end": v(-59.77, 5.97) * mm});
            skArc(sketch, "E57.4.0", {"start": v(-61.27, 2.56) * mm, "mid": v(-60.47, 1.9) * mm, "end": v(-59.47, 1.63) * mm});
            skArc(sketch, "E57.4.1", {"start": v(-61.17, 2.91) * mm, "mid": v(-60.15, 3.09) * mm, "end": v(-59.15, 2.84) * mm});
            skLineSegment(sketch, "E57.4.2", {"start": v(-61.27, 2.56) * mm, "end": v(-61.17, 2.91) * mm});
            skArc(sketch, "E57.5.0", {"start": v(-61.55, -0.8) * mm, "mid": v(-60.58, -1.17) * mm, "end": v(-59.55, -1.12) * mm});
            skArc(sketch, "E57.5.1", {"start": v(-61.57, -0.43) * mm, "mid": v(-60.65, 0.06) * mm, "end": v(-59.62, 0.13) * mm});
            skLineSegment(sketch, "E57.5.2", {"start": v(-61.55, -0.8) * mm, "end": v(-61.57, -0.43) * mm});
            skArc(sketch, "E57.6.0", {"start": v(-60.78, -4.07) * mm, "mid": v(-59.74, -4.13) * mm, "end": v(-58.78, -3.76) * mm});
            skArc(sketch, "E57.6.1", {"start": v(-60.9, -3.72) * mm, "mid": v(-60.19, -2.98) * mm, "end": v(-59.23, -2.6) * mm});
            skLineSegment(sketch, "E57.6.2", {"start": v(-60.78, -4.07) * mm, "end": v(-60.9, -3.72) * mm});
            skArc(sketch, "E57.7.0", {"start": v(-59.03, -6.94) * mm, "mid": v(-58.03, -6.68) * mm, "end": v(-57.23, -6.04) * mm});
            skArc(sketch, "E57.7.1", {"start": v(-59.26, -6.66) * mm, "mid": v(-58.8, -5.73) * mm, "end": v(-58.02, -5.07) * mm});
            skLineSegment(sketch, "E57.7.2", {"start": v(-59.03, -6.94) * mm, "end": v(-59.26, -6.66) * mm});
            skArc(sketch, "E57.8.0", {"start": v(-56.48, -9.14) * mm, "mid": v(-55.62, -8.58) * mm, "end": v(-55.05, -7.72) * mm});
            skArc(sketch, "E57.8.1", {"start": v(-56.8, -8.94) * mm, "mid": v(-56.65, -7.92) * mm, "end": v(-56.1, -7.04) * mm});
            skLineSegment(sketch, "E57.8.2", {"start": v(-56.48, -9.14) * mm, "end": v(-56.8, -8.94) * mm});
            skArc(sketch, "E57.9.0", {"start": v(-53.38, -10.44) * mm, "mid": v(-52.73, -9.64) * mm, "end": v(-52.45, -8.65) * mm});
            skArc(sketch, "E57.9.1", {"start": v(-53.74, -10.35) * mm, "mid": v(-53.91, -9.33) * mm, "end": v(-53.66, -8.33) * mm});
            skLineSegment(sketch, "E57.9.2", {"start": v(-53.38, -10.44) * mm, "end": v(-53.74, -10.35) * mm});
            skArc(sketch, "E57.10.0", {"start": v(-50.03, -10.72) * mm, "mid": v(-49.66, -9.76) * mm, "end": v(-49.7, -8.73) * mm});
            skArc(sketch, "E57.10.1", {"start": v(-50.4, -10.74) * mm, "mid": v(-50.88, -9.83) * mm, "end": v(-50.95, -8.8) * mm});
            skLineSegment(sketch, "E57.10.2", {"start": v(-50.03, -10.72) * mm, "end": v(-50.4, -10.74) * mm});
            skArc(sketch, "E57.11.0", {"start": v(-46.76, -9.95) * mm, "mid": v(-46.7, -8.92) * mm, "end": v(-47.06, -7.95) * mm});
            skArc(sketch, "E57.11.1", {"start": v(-47.1, -10.08) * mm, "mid": v(-47.84, -9.36) * mm, "end": v(-48.23, -8.4) * mm});
            skLineSegment(sketch, "E57.11.2", {"start": v(-46.76, -9.95) * mm, "end": v(-47.1, -10.08) * mm});
            skArc(sketch, "E57.12.0", {"start": v(-43.88, -8.2) * mm, "mid": v(-44.14, -7.2) * mm, "end": v(-44.79, -6.4) * mm});
            skArc(sketch, "E57.12.1", {"start": v(-44.17, -8.44) * mm, "mid": v(-45.1, -7.98) * mm, "end": v(-45.76, -7.2) * mm});
            skLineSegment(sketch, "E57.12.2", {"start": v(-43.88, -8.2) * mm, "end": v(-44.17, -8.44) * mm});
            skArc(sketch, "E57.13.0", {"start": v(-41.69, -5.66) * mm, "mid": v(-42.24, -4.8) * mm, "end": v(-43.1, -4.22) * mm});
            skArc(sketch, "E57.13.1", {"start": v(-41.88, -5.97) * mm, "mid": v(-42.9, -5.82) * mm, "end": v(-43.78, -5.27) * mm});
            skLineSegment(sketch, "E57.13.2", {"start": v(-41.69, -5.66) * mm, "end": v(-41.88, -5.97) * mm});
            skArc(sketch, "E57.14.0", {"start": v(-40.38, -2.56) * mm, "mid": v(-41.18, -1.9) * mm, "end": v(-42.18, -1.63) * mm});
            skArc(sketch, "E57.14.1", {"start": v(-40.48, -2.91) * mm, "mid": v(-41.5, -3.09) * mm, "end": v(-42.5, -2.84) * mm});
            skLineSegment(sketch, "E57.14.2", {"start": v(-40.38, -2.56) * mm, "end": v(-40.48, -2.91) * mm});
            skArc(sketch, "E57.15.0", {"start": v(-40.1, 0.8) * mm, "mid": v(-41.07, 1.17) * mm, "end": v(-42.1, 1.12) * mm});
            skArc(sketch, "E57.15.1", {"start": v(-40.08, 0.43) * mm, "mid": v(-41, -0.06) * mm, "end": v(-42.03, -0.13) * mm});
            skLineSegment(sketch, "E57.15.2", {"start": v(-40.1, 0.8) * mm, "end": v(-40.08, 0.43) * mm});
            skArc(sketch, "E57.16.0", {"start": v(-40.87, 4.07) * mm, "mid": v(-41.9, 4.13) * mm, "end": v(-42.87, 3.76) * mm});
            skArc(sketch, "E57.16.1", {"start": v(-40.74, 3.72) * mm, "mid": v(-41.46, 2.98) * mm, "end": v(-42.42, 2.6) * mm});
            skLineSegment(sketch, "E57.16.2", {"start": v(-40.87, 4.07) * mm, "end": v(-40.74, 3.72) * mm});
            skArc(sketch, "E57.17.0", {"start": v(-42.62, 6.94) * mm, "mid": v(-43.62, 6.68) * mm, "end": v(-44.42, 6.04) * mm});
            skArc(sketch, "E57.17.1", {"start": v(-42.38, 6.66) * mm, "mid": v(-42.84, 5.73) * mm, "end": v(-43.63, 5.07) * mm});
            skLineSegment(sketch, "E57.17.2", {"start": v(-42.62, 6.94) * mm, "end": v(-42.38, 6.66) * mm});
            skArc(sketch, "E57.18.0", {"start": v(-45.17, 9.14) * mm, "mid": v(-46.03, 8.58) * mm, "end": v(-46.6, 7.72) * mm});
            skArc(sketch, "E57.18.1", {"start": v(-44.86, 8.94) * mm, "mid": v(-45, 7.92) * mm, "end": v(-45.55, 7.04) * mm});
            skLineSegment(sketch, "E57.18.2", {"start": v(-45.17, 9.14) * mm, "end": v(-44.86, 8.94) * mm});
            skArc(sketch, "E57.19.0", {"start": v(-48.27, 10.44) * mm, "mid": v(-48.92, 9.64) * mm, "end": v(-49.2, 8.65) * mm});
            skArc(sketch, "E57.19.1", {"start": v(-47.91, 10.35) * mm, "mid": v(-47.73, 9.33) * mm, "end": v(-47.99, 8.33) * mm});
            skLineSegment(sketch, "E57.19.2", {"start": v(-48.27, 10.44) * mm, "end": v(-47.91, 10.35) * mm});
            skArc(sketch, "E58.trimOffspring", {"start": v(-56.86, 6.4) * mm, "mid": v(-57.39, 5.86) * mm, "end": v(-57.87, 5.27) * mm});
            skArc(sketch, "E59.trimOffspring", {"start": v(-58.54, 4.22) * mm, "mid": v(-58.88, 3.54) * mm, "end": v(-59.15, 2.84) * mm});
            skArc(sketch, "E60.trimOffspring", {"start": v(-59.47, 1.63) * mm, "mid": v(-59.58, 0.88) * mm, "end": v(-59.62, 0.13) * mm});
            skArc(sketch, "E61.trimOffspring", {"start": v(-59.55, -1.12) * mm, "mid": v(-59.42, -1.87) * mm, "end": v(-59.23, -2.6) * mm});
            skArc(sketch, "E62.trimOffspring", {"start": v(-58.78, -3.76) * mm, "mid": v(-58.42, -4.43) * mm, "end": v(-58.02, -5.07) * mm});
            skArc(sketch, "E63.trimOffspring", {"start": v(-57.23, -6.04) * mm, "mid": v(-56.68, -6.56) * mm, "end": v(-56.1, -7.04) * mm});
            skArc(sketch, "E64.trimOffspring", {"start": v(-52.45, -8.65) * mm, "mid": v(-51.7, -8.75) * mm, "end": v(-50.95, -8.8) * mm});
            skArc(sketch, "E65.trimOffspring", {"start": v(-47.06, -7.95) * mm, "mid": v(-46.4, -7.6) * mm, "end": v(-45.76, -7.2) * mm});
            skArc(sketch, "E66.trimOffspring", {"start": v(-49.7, -8.73) * mm, "mid": v(-48.96, -8.6) * mm, "end": v(-48.23, -8.4) * mm});
            skArc(sketch, "E67.trimOffspring", {"start": v(-51.95, 8.73) * mm, "mid": v(-52.7, 8.6) * mm, "end": v(-53.42, 8.4) * mm});
            skArc(sketch, "E68.trimOffspring", {"start": v(-49.2, 8.65) * mm, "mid": v(-49.94, 8.75) * mm, "end": v(-50.7, 8.8) * mm});
            skArc(sketch, "E69.trimOffspring", {"start": v(-46.6, 7.72) * mm, "mid": v(-47.28, 8.05) * mm, "end": v(-47.99, 8.33) * mm});
            skArc(sketch, "E70.trimOffspring", {"start": v(-44.42, 6.04) * mm, "mid": v(-44.97, 6.56) * mm, "end": v(-45.55, 7.04) * mm});
            skArc(sketch, "E71.trimOffspring", {"start": v(-42.87, 3.76) * mm, "mid": v(-43.22, 4.43) * mm, "end": v(-43.63, 5.07) * mm});
            skArc(sketch, "E72.trimOffspring", {"start": v(-42.1, 1.12) * mm, "mid": v(-42.23, 1.87) * mm, "end": v(-42.42, 2.6) * mm});
            skArc(sketch, "E73.trimOffspring", {"start": v(-42.18, -1.63) * mm, "mid": v(-42.07, -0.88) * mm, "end": v(-42.03, -0.13) * mm});
            skArc(sketch, "E74.trimOffspring", {"start": v(-43.1, -4.22) * mm, "mid": v(-42.77, -3.54) * mm, "end": v(-42.5, -2.84) * mm});
            skArc(sketch, "E75.trimOffspring", {"start": v(-44.79, -6.4) * mm, "mid": v(-44.26, -5.86) * mm, "end": v(-43.78, -5.27) * mm});
            skArc(sketch, "E76", {"start": v(-55.05, -7.72) * mm, "mid": v(-54.37, -8.05) * mm, "end": v(-53.66, -8.33) * mm});
            skArc(sketch, "E77.trimOffspring", {"start": v(-62.13, 7.9) * mm, "mid": v(-62.43, 7.46) * mm, "end": v(-62.71, 7) * mm});
            skArc(sketch, "E78.trimOffspring", {"start": v(-63.53, 5.39) * mm, "mid": v(-63.73, 4.89) * mm, "end": v(-63.9, 4.38) * mm});
            skArc(sketch, "E79.trimOffspring", {"start": v(-64.37, 2.63) * mm, "mid": v(-64.46, 2.1) * mm, "end": v(-64.53, 1.57) * mm});
            skArc(sketch, "E80.trimOffspring", {"start": v(-64.62, -0.25) * mm, "mid": v(-64.6, -0.78) * mm, "end": v(-64.56, -1.32) * mm});
            skArc(sketch, "E81.trimOffspring", {"start": v(-64.27, -3.1) * mm, "mid": v(-64.14, -3.63) * mm, "end": v(-63.99, -4.14) * mm});
            skArc(sketch, "E82.trimOffspring", {"start": v(-63.33, -5.84) * mm, "mid": v(-63.1, -6.32) * mm, "end": v(-62.84, -6.79) * mm});
            skArc(sketch, "E83.trimOffspring", {"start": v(-61.84, -8.3) * mm, "mid": v(-61.5, -8.73) * mm, "end": v(-61.16, -9.14) * mm});
            skArc(sketch, "E84.trimOffspring", {"start": v(-59.87, -10.42) * mm, "mid": v(-59.46, -10.76) * mm, "end": v(-59.04, -11.09) * mm});
            skArc(sketch, "E85.trimOffspring", {"start": v(-57.5, -12.07) * mm, "mid": v(-57.04, -12.32) * mm, "end": v(-56.55, -12.55) * mm});
            skArc(sketch, "E86.trimOffspring", {"start": v(-54.85, -13.2) * mm, "mid": v(-54.34, -13.34) * mm, "end": v(-53.82, -13.47) * mm});
            skArc(sketch, "E87.trimOffspring", {"start": v(-52.02, -13.75) * mm, "mid": v(-51.49, -13.78) * mm, "end": v(-50.95, -13.8) * mm});
            skArc(sketch, "E88.trimOffspring", {"start": v(-49.14, -13.7) * mm, "mid": v(-48.6, -13.62) * mm, "end": v(-48.08, -13.52) * mm});
            skArc(sketch, "E89.trimOffspring", {"start": v(-46.33, -13.04) * mm, "mid": v(-45.82, -12.86) * mm, "end": v(-45.33, -12.66) * mm});
            skArc(sketch, "E90.trimOffspring", {"start": v(-43.71, -11.82) * mm, "mid": v(-43.26, -11.54) * mm, "end": v(-42.82, -11.24) * mm});
            skArc(sketch, "E91.trimOffspring", {"start": v(-41.41, -10.09) * mm, "mid": v(-41.03, -9.71) * mm, "end": v(-40.66, -9.33) * mm});
            skArc(sketch, "E92.trimOffspring", {"start": v(-39.52, -7.9) * mm, "mid": v(-39.22, -7.46) * mm, "end": v(-38.94, -7) * mm});
            skArc(sketch, "E93.trimOffspring", {"start": v(-38.12, -5.39) * mm, "mid": v(-37.92, -4.89) * mm, "end": v(-37.74, -4.38) * mm});
            skArc(sketch, "E94.trimOffspring", {"start": v(-37.28, -2.63) * mm, "mid": v(-37.19, -2.1) * mm, "end": v(-37.12, -1.57) * mm});
            skArc(sketch, "E95.trimOffspring", {"start": v(-37.03, 0.25) * mm, "mid": v(-37.05, 0.78) * mm, "end": v(-37.09, 1.32) * mm});
            skArc(sketch, "E96.trimOffspring", {"start": v(-37.38, 3.1) * mm, "mid": v(-37.51, 3.63) * mm, "end": v(-37.66, 4.14) * mm});
            skArc(sketch, "E97.trimOffspring", {"start": v(-38.32, 5.84) * mm, "mid": v(-38.56, 6.32) * mm, "end": v(-38.81, 6.79) * mm});
            skArc(sketch, "E98.trimOffspring", {"start": v(-39.8, 8.3) * mm, "mid": v(-40.14, 8.73) * mm, "end": v(-40.49, 9.14) * mm});
            skArc(sketch, "E99.trimOffspring", {"start": v(-41.78, 10.42) * mm, "mid": v(-42.19, 10.76) * mm, "end": v(-42.61, 11.09) * mm});
            skArc(sketch, "E100.trimOffspring", {"start": v(-44.14, 12.07) * mm, "mid": v(-44.61, 12.32) * mm, "end": v(-45.1, 12.55) * mm});
            skArc(sketch, "E101.trimOffspring", {"start": v(-46.8, 13.2) * mm, "mid": v(-47.31, 13.34) * mm, "end": v(-47.83, 13.47) * mm});
            skArc(sketch, "E102.trimOffspring", {"start": v(-49.63, 13.75) * mm, "mid": v(-50.16, 13.78) * mm, "end": v(-50.7, 13.8) * mm});
            skArc(sketch, "E103.trimOffspring", {"start": v(-52.51, 13.7) * mm, "mid": v(-53.04, 13.62) * mm, "end": v(-53.57, 13.52) * mm});
            skArc(sketch, "E104.trimOffspring", {"start": v(-55.32, 13.04) * mm, "mid": v(-55.83, 12.86) * mm, "end": v(-56.32, 12.66) * mm});
            skArc(sketch, "E105.trimOffspring", {"start": v(-57.94, 11.82) * mm, "mid": v(-58.4, 11.54) * mm, "end": v(-58.83, 11.24) * mm});
            skArc(sketch, "E106", {"start": v(-55.18, 7.65) * mm, "mid": v(-55.54, 7.43) * mm, "end": v(-55.9, 7.2) * mm});
            skSolve(sketch);
        }
        {
            var Q0;
            Q0=qCreatedBy(makeId("Front.planeOp"),FACE);
            var sketch = newSketch(context, id + "F1", { "sketchPlane" : qUnion([Q0])});
            skLineSegment(sketch, "E107", {"start": v(-1, -41.23) * mm, "end": v(-1, -14.33) * mm, "construction": true});
            skLineSegment(sketch, "E108", {"start": v(-1, -41.23) * mm, "end": v(-2.5, -14.7) * mm, "construction": true});
            skLineSegment(sketch, "E109", {"start": v(-1, -26.23) * mm, "end": v(-17.94, -32.4) * mm, "construction": true});
            skCircle(sketch, "E110", {"center": v(-3.25, -27.32) * mm, "radius": 2.5 * mm, "construction": true});
            skPoint(sketch, "E111.center", {"position": v(-1, -41.23) * mm});
            skCircle(sketch, "E112", {"center": v(-1, -41.23) * mm, "radius": 1.5 * mm});
            skCircle(sketch, "E113", {"center": v(-1, -26.23) * mm, "radius": 2.5 * mm, "construction": true});
            skLineSegment(sketch, "E111.21.1", {"start": v(14.31, -44.9) * mm, "end": v(14.14, -45.58) * mm});
            skArc(sketch, "E111.3.0", {"start": v(-11.23, -29.26) * mm, "mid": v(-11.09, -30.32) * mm, "end": v(-10.5, -31.22) * mm});
            skLineSegment(sketch, "E111.24.1", {"start": v(13.55, -35.2) * mm, "end": v(13.8, -35.85) * mm});
            skArc(sketch, "E111.13.2", {"start": v(-6.9, -55.83) * mm, "mid": v(-7.1, -54.77) * mm, "end": v(-6.84, -53.73) * mm});
            skLineSegment(sketch, "E111.16.1", {"start": v(3.48, -56.33) * mm, "end": v(2.8, -56.51) * mm});
            skArc(sketch, "E111.21.2", {"start": v(14.14, -45.58) * mm, "mid": v(13.1, -45.88) * mm, "end": v(12.04, -45.73) * mm});
            skLineSegment(sketch, "E111.3.1", {"start": v(-11.23, -29.26) * mm, "end": v(-10.7, -28.82) * mm});
            skLineSegment(sketch, "E111.22.1", {"start": v(14.74, -41.64) * mm, "end": v(14.7, -42.33) * mm});
            skArc(sketch, "E111.24.2", {"start": v(13.8, -35.85) * mm, "mid": v(13.15, -36.7) * mm, "end": v(12.2, -37.2) * mm});
            skArc(sketch, "E111.11.2", {"start": v(-12.33, -52.17) * mm, "mid": v(-12.08, -51.12) * mm, "end": v(-11.42, -50.28) * mm});
            skLineSegment(sketch, "E111.11.1", {"start": v(-11.84, -52.66) * mm, "end": v(-12.33, -52.17) * mm});
            skArc(sketch, "E111.22.0", {"start": v(14.74, -41.64) * mm, "mid": v(13.85, -41.04) * mm, "end": v(12.8, -40.86) * mm});
            skArc(sketch, "E111.3.2", {"start": v(-10.7, -28.82) * mm, "mid": v(-9.68, -29.17) * mm, "end": v(-8.91, -29.92) * mm});
            skArc(sketch, "E111.22.2", {"start": v(14.7, -42.33) * mm, "mid": v(13.77, -42.85) * mm, "end": v(12.7, -42.92) * mm});
            skLineSegment(sketch, "E111.17.1", {"start": v(6.52, -55.07) * mm, "end": v(5.9, -55.39) * mm});
            skLineSegment(sketch, "E111.25.1", {"start": v(11.98, -32.3) * mm, "end": v(12.36, -32.89) * mm});
            skLineSegment(sketch, "E111.12.1", {"start": v(-9.23, -54.66) * mm, "end": v(-9.81, -54.28) * mm});
            skArc(sketch, "E111.1.0", {"start": v(-5.48, -26.13) * mm, "mid": v(-5.78, -27.16) * mm, "end": v(-5.61, -28.22) * mm});
            skArc(sketch, "E114", {"start": v(-13.86, -46.23) * mm, "mid": v(-12.81, -48.36) * mm, "end": v(-11.42, -50.28) * mm});
            skCircle(sketch, "E115", {"center": v(-1, -41.23) * mm, "radius": 15 * mm, "construction": true});
            skCircle(sketch, "E116", {"center": v(-1, -41.23) * mm, "radius": 15.75 * mm, "construction": true});
            skCircle(sketch, "E117", {"center": v(-1, -41.23) * mm, "radius": 14.1 * mm, "construction": true});
            skLineSegment(sketch, "E118", {"start": v(-1, -26.23) * mm, "end": v(-10, -26.23) * mm, "construction": true});
            skArc(sketch, "E111.15.0", {"start": v(0.24, -56.93) * mm, "mid": v(0.74, -55.98) * mm, "end": v(0.8, -54.9) * mm});
            skLineSegment(sketch, "E111.20.1", {"start": v(13.22, -48) * mm, "end": v(12.9, -48.63) * mm});
            skArc(sketch, "E111.18.0", {"start": v(9.23, -53.2) * mm, "mid": v(9.08, -52.14) * mm, "end": v(8.5, -51.24) * mm});
            skArc(sketch, "E111.12.2", {"start": v(-9.81, -54.28) * mm, "mid": v(-9.79, -53.2) * mm, "end": v(-9.3, -52.25) * mm});
            skLineSegment(sketch, "E111.15.1", {"start": v(0.24, -56.93) * mm, "end": v(-0.46, -56.97) * mm});
            skArc(sketch, "E111.4.2", {"start": v(-13.06, -31.1) * mm, "mid": v(-12, -31.24) * mm, "end": v(-11.1, -31.82) * mm});
            skArc(sketch, "E111.26.0", {"start": v(9.84, -29.8) * mm, "mid": v(8.8, -30.06) * mm, "end": v(7.96, -30.73) * mm});
            skArc(sketch, "E111.20.2", {"start": v(12.9, -48.63) * mm, "mid": v(11.83, -48.71) * mm, "end": v(10.82, -48.34) * mm});
            skLineSegment(sketch, "E111.18.1", {"start": v(9.23, -53.2) * mm, "end": v(8.7, -53.64) * mm});
            skArc(sketch, "E111.13.0", {"start": v(-6.25, -56.08) * mm, "mid": v(-5.4, -55.42) * mm, "end": v(-4.92, -54.46) * mm});
            skLineSegment(sketch, "E111.26.1", {"start": v(9.84, -29.8) * mm, "end": v(10.33, -30.3) * mm});
            skArc(sketch, "E111.21.0", {"start": v(14.31, -44.9) * mm, "mid": v(13.57, -44.13) * mm, "end": v(12.57, -43.74) * mm});
            skArc(sketch, "E111.24.0", {"start": v(13.55, -35.2) * mm, "mid": v(12.49, -35.01) * mm, "end": v(11.45, -35.29) * mm});
            skArc(sketch, "E111.18.2", {"start": v(8.7, -53.64) * mm, "mid": v(7.68, -53.29) * mm, "end": v(6.9, -52.53) * mm});
            skLineSegment(sketch, "E111.13.1", {"start": v(-6.25, -56.08) * mm, "end": v(-6.9, -55.83) * mm});
            skArc(sketch, "E111.16.0", {"start": v(3.48, -56.33) * mm, "mid": v(3.77, -55.3) * mm, "end": v(3.6, -54.23) * mm});
            skArc(sketch, "E111.26.2", {"start": v(10.33, -30.3) * mm, "mid": v(10.08, -31.34) * mm, "end": v(9.41, -32.18) * mm});
            skArc(sketch, "E111.19.0", {"start": v(11.5, -50.81) * mm, "mid": v(11.13, -49.8) * mm, "end": v(10.37, -49.04) * mm});
            skArc(sketch, "E111.29.2", {"start": v(1.74, -25.72) * mm, "mid": v(2.15, -26.71) * mm, "end": v(2.1, -27.79) * mm});
            skArc(sketch, "E111.11.0", {"start": v(-11.84, -52.66) * mm, "mid": v(-10.8, -52.4) * mm, "end": v(-9.96, -51.72) * mm});
            skArc(sketch, "E111.27.0", {"start": v(7.22, -27.8) * mm, "mid": v(6.26, -28.27) * mm, "end": v(5.58, -29.1) * mm});
            skArc(sketch, "E111.17.0", {"start": v(6.52, -55.07) * mm, "mid": v(6.6, -54) * mm, "end": v(6.21, -53) * mm});
            skLineSegment(sketch, "E111.19.1", {"start": v(11.5, -50.81) * mm, "end": v(11.06, -51.36) * mm});
            skArc(sketch, "E111.14.0", {"start": v(-3.05, -56.85) * mm, "mid": v(-2.36, -56.02) * mm, "end": v(-2.08, -54.99) * mm});
            skArc(sketch, "E111.27.2", {"start": v(7.8, -28.18) * mm, "mid": v(7.78, -29.25) * mm, "end": v(7.3, -30.21) * mm});
            skLineSegment(sketch, "E111.27.1", {"start": v(7.22, -27.8) * mm, "end": v(7.8, -28.18) * mm});
            skArc(sketch, "E111.25.0", {"start": v(11.98, -32.3) * mm, "mid": v(10.9, -32.34) * mm, "end": v(9.94, -32.83) * mm});
            skArc(sketch, "E111.19.2", {"start": v(11.06, -51.36) * mm, "mid": v(10, -51.22) * mm, "end": v(9.09, -50.64) * mm});
            skArc(sketch, "E111.12.0", {"start": v(-9.23, -54.66) * mm, "mid": v(-8.26, -54.2) * mm, "end": v(-7.58, -53.36) * mm});
            skLineSegment(sketch, "E111.14.1", {"start": v(-3.05, -56.85) * mm, "end": v(-3.74, -56.74) * mm});
            skArc(sketch, "E111.28.0", {"start": v(4.25, -26.38) * mm, "mid": v(3.4, -27.04) * mm, "end": v(2.91, -28) * mm});
            skArc(sketch, "E111.4.0", {"start": v(-13.5, -31.65) * mm, "mid": v(-13.13, -32.66) * mm, "end": v(-12.38, -33.42) * mm});
            skArc(sketch, "E111.23.0", {"start": v(14.48, -38.35) * mm, "mid": v(13.49, -37.95) * mm, "end": v(12.41, -38) * mm});
            skArc(sketch, "E111.17.2", {"start": v(5.9, -55.39) * mm, "mid": v(4.98, -54.83) * mm, "end": v(4.39, -53.93) * mm});
            skArc(sketch, "E111.20.0", {"start": v(13.22, -48) * mm, "mid": v(12.65, -47.1) * mm, "end": v(11.75, -46.5) * mm});
            skArc(sketch, "E111.14.2", {"start": v(-3.74, -56.74) * mm, "mid": v(-4.15, -55.75) * mm, "end": v(-4.11, -54.67) * mm});
            skLineSegment(sketch, "E111.28.1", {"start": v(4.25, -26.38) * mm, "end": v(4.9, -26.63) * mm});
            skLineSegment(sketch, "E111.1.1", {"start": v(-5.48, -26.13) * mm, "end": v(-4.8, -25.95) * mm});
            skArc(sketch, "E111.28.2", {"start": v(4.9, -26.63) * mm, "mid": v(5.1, -27.69) * mm, "end": v(4.83, -28.73) * mm});
            skLineSegment(sketch, "E111.4.1", {"start": v(-13.5, -31.65) * mm, "end": v(-13.06, -31.1) * mm});
            skArc(sketch, "E111.2.0", {"start": v(-8.52, -27.4) * mm, "mid": v(-8.6, -28.46) * mm, "end": v(-8.22, -29.47) * mm});
            skLineSegment(sketch, "E111.23.1", {"start": v(14.48, -38.35) * mm, "end": v(14.6, -39.04) * mm});
            skLineSegment(sketch, "E111.2.1", {"start": v(-8.52, -27.4) * mm, "end": v(-7.9, -27.07) * mm});
            skArc(sketch, "E111.23.2", {"start": v(14.6, -39.04) * mm, "mid": v(13.78, -39.74) * mm, "end": v(12.74, -40.03) * mm});
            skArc(sketch, "E111.15.2", {"start": v(-0.46, -56.97) * mm, "mid": v(-1.07, -56.08) * mm, "end": v(-1.25, -55.03) * mm});
            skArc(sketch, "E111.2.2", {"start": v(-7.9, -27.07) * mm, "mid": v(-6.99, -27.63) * mm, "end": v(-6.39, -28.53) * mm});
            skLineSegment(sketch, "E111.29.1", {"start": v(1.05, -25.61) * mm, "end": v(1.74, -25.72) * mm});
            skArc(sketch, "E111.16.2", {"start": v(2.8, -56.51) * mm, "mid": v(2.02, -55.77) * mm, "end": v(1.63, -54.78) * mm});
            skArc(sketch, "E111.1.2", {"start": v(-4.8, -25.95) * mm, "mid": v(-4.03, -26.69) * mm, "end": v(-3.63, -27.68) * mm});
            skArc(sketch, "E119", {"start": v(-1.55, -25.49) * mm, "mid": v(-0.94, -26.37) * mm, "end": v(-0.76, -27.43) * mm});
            skArc(sketch, "E120.MirrorCS", {"start": v(-2.24, -25.53) * mm, "mid": v(-2.75, -26.48) * mm, "end": v(-2.8, -27.55) * mm});
            skLineSegment(sketch, "E121", {"start": v(-2.24, -25.53) * mm, "end": v(-1.55, -25.49) * mm});
            skArc(sketch, "E111.25.2", {"start": v(12.36, -32.89) * mm, "mid": v(11.9, -33.86) * mm, "end": v(11.07, -34.54) * mm});
            skArc(sketch, "E111.29.0", {"start": v(1.05, -25.61) * mm, "mid": v(0.36, -26.44) * mm, "end": v(0.08, -27.47) * mm});
            skLineSegment(sketch, "E122", {"start": v(-1, -41.23) * mm, "end": v(-101, -41.23) * mm, "construction": true});
            skCircle(sketch, "E123", {"center": v(-101, -41.23) * mm, "radius": 1.5 * mm});
            skArc(sketch, "E124", {"start": v(-101, -36.23) * mm, "mid": v(-106, -41.23) * mm, "end": v(-101, -46.23) * mm});
            skCircle(sketch, "E125", {"center": v(-1, -41.23) * mm, "radius": 5 * mm});
            skLineSegment(sketch, "E126", {"start": v(-101, -36.23) * mm, "end": v(-13.86, -36.23) * mm});
            skLineSegment(sketch, "E127", {"start": v(-101, -46.23) * mm, "end": v(-13.86, -46.23) * mm});
            skLineSegment(sketch, "E128", {"start": v(-1.75, -88.05) * mm, "end": v(-1.75, -69.5) * mm, "construction": true});
            skLineSegment(sketch, "E129", {"start": v(-1.75, -88.05) * mm, "end": v(-2.8, -69.5) * mm, "construction": true});
            skLineSegment(sketch, "E130", {"start": v(-1.75, -78.05) * mm, "end": v(-17.98, -83.95) * mm, "construction": true});
            skLineSegment(sketch, "E131", {"start": v(-1.75, -78.05) * mm, "end": v(-18.57, -78.05) * mm, "construction": true});
            skCircle(sketch, "E132", {"center": v(-1.75, -78.05) * mm, "radius": 2.5 * mm, "construction": true});
            skCircle(sketch, "E133", {"center": v(-1.75, -88.05) * mm, "radius": 1.5 * mm});
            skCircle(sketch, "E134", {"center": v(-4.09, -78.94) * mm, "radius": 2.5 * mm, "construction": true});
            skCircle(sketch, "E135", {"center": v(-1.75, -88.05) * mm, "radius": 10.75 * mm, "construction": true});
            skArc(sketch, "E136.13.2", {"start": v(7.38, -93.72) * mm, "mid": v(6.83, -92.84) * mm, "end": v(5.98, -92.25) * mm});
            skArc(sketch, "E136.16.2", {"start": v(8.2, -84) * mm, "mid": v(7.17, -83.92) * mm, "end": v(6.19, -84.26) * mm});
            skArc(sketch, "E136.14.0", {"start": v(8.6, -90.94) * mm, "mid": v(7.58, -91.14) * mm, "end": v(6.57, -90.9) * mm});
            skArc(sketch, "E136.8.2", {"start": v(-7.43, -97.17) * mm, "mid": v(-6.54, -96.63) * mm, "end": v(-5.96, -95.77) * mm});
            skArc(sketch, "E136.11.2", {"start": v(2.3, -98) * mm, "mid": v(2.38, -96.97) * mm, "end": v(2.03, -95.99) * mm});
            skArc(sketch, "E136.14.2", {"start": v(8.68, -90.62) * mm, "mid": v(7.9, -89.95) * mm, "end": v(6.9, -89.65) * mm});
            skArc(sketch, "E136.19.2", {"start": v(0.82, -77.6) * mm, "mid": v(0.15, -78.4) * mm, "end": v(-0.14, -79.4) * mm});
            skArc(sketch, "E136.9.0", {"start": v(-4.65, -98.4) * mm, "mid": v(-4.85, -97.38) * mm, "end": v(-4.61, -96.37) * mm});
            skArc(sketch, "E136.9.2", {"start": v(-4.33, -98.48) * mm, "mid": v(-3.66, -97.7) * mm, "end": v(-3.36, -96.7) * mm});
            skArc(sketch, "E136.12.0", {"start": v(4.92, -96.47) * mm, "mid": v(3.98, -96.03) * mm, "end": v(3.3, -95.25) * mm});
            skCircle(sketch, "E137", {"center": v(-1.75, -88.05) * mm, "radius": 9.4 * mm, "construction": true});
            skArc(sketch, "E136.10.0", {"start": v(-1.3, -98.79) * mm, "mid": v(-1.81, -97.88) * mm, "end": v(-1.9, -96.84) * mm});
            skArc(sketch, "E136.7.0", {"start": v(-10.18, -94.72) * mm, "mid": v(-9.74, -93.78) * mm, "end": v(-8.96, -93.1) * mm});
            skArc(sketch, "E136.1.2", {"start": v(-5.8, -78.09) * mm, "mid": v(-5.88, -79.12) * mm, "end": v(-5.54, -80.1) * mm});
            skArc(sketch, "E136.17.2", {"start": v(6.47, -81.12) * mm, "mid": v(5.46, -81.36) * mm, "end": v(4.63, -82) * mm});
            skArc(sketch, "E136.2.0", {"start": v(-8.43, -79.62) * mm, "mid": v(-7.49, -80.06) * mm, "end": v(-6.8, -80.84) * mm});
            skArc(sketch, "E138", {"start": v(-9.59, -92.05) * mm, "mid": v(-9.3, -92.58) * mm, "end": v(-8.96, -93.1) * mm});
            skArc(sketch, "E136.18.0", {"start": v(4.2, -79.1) * mm, "mid": v(4.07, -80.13) * mm, "end": v(3.54, -81.02) * mm});
            skArc(sketch, "E136.12.2", {"start": v(5.17, -96.27) * mm, "mid": v(4.93, -95.26) * mm, "end": v(4.3, -94.43) * mm});
            skArc(sketch, "E136.16.0", {"start": v(8.32, -84.3) * mm, "mid": v(7.61, -85.06) * mm, "end": v(6.66, -85.47) * mm});
            skCircle(sketch, "E139", {"center": v(-1.75, -88.05) * mm, "radius": 10 * mm, "construction": true});
            skArc(sketch, "E136.13.0", {"start": v(7.2, -94) * mm, "mid": v(6.17, -93.87) * mm, "end": v(5.28, -93.34) * mm});
            skArc(sketch, "E136.7.2", {"start": v(-9.97, -94.97) * mm, "mid": v(-8.96, -94.73) * mm, "end": v(-8.14, -94.1) * mm});
            skArc(sketch, "E136.10.2", {"start": v(-0.98, -98.77) * mm, "mid": v(-0.58, -97.8) * mm, "end": v(-0.61, -96.77) * mm});
            skArc(sketch, "E136.2.2", {"start": v(-8.68, -79.83) * mm, "mid": v(-8.44, -80.84) * mm, "end": v(-7.8, -81.66) * mm});
            skArc(sketch, "E136.18.2", {"start": v(3.92, -78.92) * mm, "mid": v(3.04, -79.46) * mm, "end": v(2.45, -80.32) * mm});
            skArc(sketch, "E136.8.0", {"start": v(-7.7, -97) * mm, "mid": v(-7.58, -95.97) * mm, "end": v(-7.04, -95.08) * mm});
            skArc(sketch, "E140.MirrorCS", {"start": v(-2.53, -77.32) * mm, "mid": v(-2.92, -78.28) * mm, "end": v(-2.9, -79.32) * mm});
            skArc(sketch, "E136.19.0", {"start": v(1.14, -77.7) * mm, "mid": v(1.34, -78.71) * mm, "end": v(1.1, -79.73) * mm});
            skLineSegment(sketch, "E136.8.1", {"start": v(-7.43, -97.17) * mm, "end": v(-7.7, -97) * mm});
            skLineSegment(sketch, "E136.11.1", {"start": v(2.3, -98) * mm, "end": v(1.99, -98.12) * mm});
            skLineSegment(sketch, "E136.19.1", {"start": v(0.82, -77.6) * mm, "end": v(1.14, -77.7) * mm});
            skLineSegment(sketch, "E136.9.1", {"start": v(-4.33, -98.48) * mm, "end": v(-4.65, -98.4) * mm});
            skArc(sketch, "E136.1.0", {"start": v(-5.5, -77.97) * mm, "mid": v(-4.74, -78.68) * mm, "end": v(-4.33, -79.63) * mm});
            skArc(sketch, "E136.17.0", {"start": v(6.67, -81.37) * mm, "mid": v(6.23, -82.31) * mm, "end": v(5.45, -83) * mm});
            skLineSegment(sketch, "E136.14.1", {"start": v(8.68, -90.62) * mm, "end": v(8.6, -90.94) * mm});
            skLineSegment(sketch, "E136.1.1", {"start": v(-5.8, -78.09) * mm, "end": v(-5.5, -77.97) * mm});
            skArc(sketch, "E136.15.0", {"start": v(8.99, -87.6) * mm, "mid": v(8.08, -88.1) * mm, "end": v(7.04, -88.2) * mm});
            skLineSegment(sketch, "E136.17.1", {"start": v(6.47, -81.12) * mm, "end": v(6.67, -81.37) * mm});
            skLineSegment(sketch, "E136.12.1", {"start": v(5.17, -96.27) * mm, "end": v(4.92, -96.47) * mm});
            skLineSegment(sketch, "E136.10.1", {"start": v(-0.98, -98.77) * mm, "end": v(-1.3, -98.79) * mm});
            skArc(sketch, "E136.15.2", {"start": v(8.97, -87.27) * mm, "mid": v(8, -86.88) * mm, "end": v(6.97, -86.9) * mm});
            skLineSegment(sketch, "E136.2.1", {"start": v(-8.68, -79.83) * mm, "end": v(-8.43, -79.62) * mm});
            skLineSegment(sketch, "E136.18.1", {"start": v(3.92, -78.92) * mm, "end": v(4.2, -79.1) * mm});
            skLineSegment(sketch, "E136.13.1", {"start": v(7.38, -93.72) * mm, "end": v(7.2, -94) * mm});
            skArc(sketch, "E136.11.0", {"start": v(1.99, -98.12) * mm, "mid": v(1.23, -97.41) * mm, "end": v(0.82, -96.46) * mm});
            skLineSegment(sketch, "E136.16.1", {"start": v(8.2, -84) * mm, "end": v(8.32, -84.3) * mm});
            skLineSegment(sketch, "E141", {"start": v(-2.53, -77.32) * mm, "end": v(-2.2, -77.3) * mm});
            skLineSegment(sketch, "E136.15.1", {"start": v(8.97, -87.27) * mm, "end": v(8.99, -87.6) * mm});
            skArc(sketch, "E142", {"start": v(-2.2, -77.3) * mm, "mid": v(-1.7, -78.21) * mm, "end": v(-1.6, -79.25) * mm});
            skLineSegment(sketch, "E136.7.1", {"start": v(-9.97, -94.97) * mm, "end": v(-10.18, -94.72) * mm});
            skLineSegment(sketch, "E143", {"start": v(-1.75, -88.05) * mm, "end": v(-26.75, -88.05) * mm, "construction": true});
            skCircle(sketch, "E144", {"center": v(-26.75, -88.05) * mm, "radius": 1.5 * mm});
            skArc(sketch, "E145", {"start": v(-26.75, -84.05) * mm, "mid": v(-30.75, -88.05) * mm, "end": v(-26.75, -92.05) * mm});
            skLineSegment(sketch, "E146", {"start": v(-26.75, -84.05) * mm, "end": v(-9.59, -84.05) * mm});
            skLineSegment(sketch, "E147", {"start": v(-26.75, -92.05) * mm, "end": v(-9.59, -92.05) * mm});
            skLineSegment(sketch, "E148.trimOffspring", {"start": v(-1.98, -84.05) * mm, "end": v(-1.75, -84.05) * mm});
            skPoint(sketch, "E149.orphan", {"position": v(-1.75, -92.05) * mm});
            skLineSegment(sketch, "E150.trimOffspring", {"start": v(-1.29, -36.23) * mm, "end": v(-1, -36.23) * mm});
            skLineSegment(sketch, "E151", {"start": v(-0.98, -116.16) * mm, "end": v(24.02, -116.16) * mm, "construction": true});
            skLineSegment(sketch, "E152", {"start": v(-0.98, -116.16) * mm, "end": v(-100.98, -116.16) * mm, "construction": true});
            skCircle(sketch, "E153", {"center": v(-100.98, -116.16) * mm, "radius": 1.5 * mm});
            skCircle(sketch, "E154", {"center": v(-0.98, -116.16) * mm, "radius": 1.5 * mm});
            skCircle(sketch, "E155", {"center": v(24.02, -116.16) * mm, "radius": 1.5 * mm});
            skCircle(sketch, "E156", {"center": v(24.02, -116.16) * mm, "radius": 4 * mm});
            skCircle(sketch, "E157", {"center": v(-100.98, -116.16) * mm, "radius": 4 * mm});
            skLineSegment(sketch, "E158", {"start": v(-0.98, -129.6) * mm, "end": v(-100.98, -129.6) * mm, "construction": true});
            skCircle(sketch, "E159", {"center": v(-100.98, -129.6) * mm, "radius": 1.5 * mm});
            skCircle(sketch, "E160", {"center": v(-0.98, -129.6) * mm, "radius": 1.5 * mm});
            skCircle(sketch, "E161", {"center": v(-0.98, -129.6) * mm, "radius": 4 * mm});
            skCircle(sketch, "E162", {"center": v(-100.98, -129.6) * mm, "radius": 4 * mm});
            skLineSegment(sketch, "E163", {"start": v(-100.98, -112.16) * mm, "end": v(24.02, -112.16) * mm});
            skLineSegment(sketch, "E164", {"start": v(24.02, -120.16) * mm, "end": v(-100.98, -120.16) * mm});
            skLineSegment(sketch, "E165", {"start": v(-100.98, -125.6) * mm, "end": v(-0.98, -125.6) * mm});
            skLineSegment(sketch, "E166", {"start": v(-0.98, -133.6) * mm, "end": v(-100.98, -133.6) * mm});
            skArc(sketch, "E167.trimOffspring", {"start": v(-12.38, -33.42) * mm, "mid": v(-13.2, -34.78) * mm, "end": v(-13.86, -36.23) * mm});
            skArc(sketch, "E168.trimOffspring", {"start": v(-10.5, -31.22) * mm, "mid": v(-10.8, -31.52) * mm, "end": v(-11.1, -31.82) * mm});
            skArc(sketch, "E169.trimOffspring", {"start": v(-8.22, -29.47) * mm, "mid": v(-8.57, -29.7) * mm, "end": v(-8.91, -29.92) * mm});
            skArc(sketch, "E170.trimOffspring", {"start": v(-5.59, -28.22) * mm, "mid": v(-6, -28.36) * mm, "end": v(-6.39, -28.53) * mm});
            skArc(sketch, "E171.trimOffspring", {"start": v(-2.8, -27.55) * mm, "mid": v(-3.22, -27.61) * mm, "end": v(-3.63, -27.68) * mm});
            skArc(sketch, "E172.trimOffspring", {"start": v(0.08, -27.47) * mm, "mid": v(-0.34, -27.45) * mm, "end": v(-0.76, -27.43) * mm});
            skArc(sketch, "E173.trimOffspring", {"start": v(2.91, -28) * mm, "mid": v(2.51, -27.89) * mm, "end": v(2.1, -27.79) * mm});
            skArc(sketch, "E174.trimOffspring", {"start": v(5.58, -29.1) * mm, "mid": v(5.2, -28.9) * mm, "end": v(4.83, -28.73) * mm});
            skArc(sketch, "E175.trimOffspring", {"start": v(7.96, -30.73) * mm, "mid": v(7.63, -30.47) * mm, "end": v(7.3, -30.21) * mm});
            skArc(sketch, "E176.trimOffspring", {"start": v(9.94, -32.83) * mm, "mid": v(9.68, -32.5) * mm, "end": v(9.41, -32.18) * mm});
            skArc(sketch, "E177.trimOffspring", {"start": v(11.45, -35.29) * mm, "mid": v(11.26, -34.91) * mm, "end": v(11.07, -34.54) * mm});
            skArc(sketch, "E178.trimOffspring", {"start": v(12.41, -38) * mm, "mid": v(12.31, -37.6) * mm, "end": v(12.2, -37.2) * mm});
            skArc(sketch, "E179.trimOffspring", {"start": v(12.8, -40.86) * mm, "mid": v(12.77, -40.45) * mm, "end": v(12.74, -40.03) * mm});
            skArc(sketch, "E180.trimOffspring", {"start": v(12.57, -43.74) * mm, "mid": v(12.64, -43.33) * mm, "end": v(12.7, -42.92) * mm});
            skArc(sketch, "E181.trimOffspring", {"start": v(11.75, -46.5) * mm, "mid": v(11.9, -46.12) * mm, "end": v(12.04, -45.73) * mm});
            skArc(sketch, "E182.trimOffspring", {"start": v(10.37, -49.04) * mm, "mid": v(10.6, -48.7) * mm, "end": v(10.82, -48.34) * mm});
            skArc(sketch, "E183.trimOffspring", {"start": v(8.5, -51.24) * mm, "mid": v(8.8, -50.94) * mm, "end": v(9.09, -50.64) * mm});
            skArc(sketch, "E184.trimOffspring", {"start": v(6.21, -53) * mm, "mid": v(6.56, -52.77) * mm, "end": v(6.9, -52.53) * mm});
            skArc(sketch, "E185.trimOffspring", {"start": v(3.6, -54.23) * mm, "mid": v(4, -54.09) * mm, "end": v(4.39, -53.93) * mm});
            skArc(sketch, "E186.trimOffspring", {"start": v(0.8, -54.9) * mm, "mid": v(1.22, -54.85) * mm, "end": v(1.63, -54.78) * mm});
            skArc(sketch, "E187.trimOffspring", {"start": v(-2.08, -54.99) * mm, "mid": v(-1.66, -55.01) * mm, "end": v(-1.25, -55.03) * mm});
            skArc(sketch, "E188.trimOffspring", {"start": v(-4.92, -54.46) * mm, "mid": v(-4.51, -54.57) * mm, "end": v(-4.11, -54.67) * mm});
            skArc(sketch, "E189.trimOffspring", {"start": v(-7.58, -53.36) * mm, "mid": v(-7.21, -53.55) * mm, "end": v(-6.84, -53.73) * mm});
            skArc(sketch, "E190.trimOffspring", {"start": v(-9.96, -51.72) * mm, "mid": v(-9.64, -52) * mm, "end": v(-9.3, -52.25) * mm});
            skArc(sketch, "E191.trimOffspring", {"start": v(-7.8, -81.66) * mm, "mid": v(-8.8, -82.78) * mm, "end": v(-9.59, -84.05) * mm});
            skArc(sketch, "E192.trimOffspring", {"start": v(-5.54, -80.1) * mm, "mid": v(-6.19, -80.45) * mm, "end": v(-6.8, -80.84) * mm});
            skArc(sketch, "E193.trimOffspring", {"start": v(-2.9, -79.32) * mm, "mid": v(-3.62, -79.45) * mm, "end": v(-4.33, -79.63) * mm});
            skArc(sketch, "E194.trimOffspring", {"start": v(-0.14, -79.4) * mm, "mid": v(-0.87, -79.3) * mm, "end": v(-1.6, -79.25) * mm});
            skArc(sketch, "E195.trimOffspring", {"start": v(2.45, -80.32) * mm, "mid": v(1.79, -80) * mm, "end": v(1.1, -79.73) * mm});
            skArc(sketch, "E196.trimOffspring", {"start": v(4.63, -82) * mm, "mid": v(4.1, -81.48) * mm, "end": v(3.54, -81.02) * mm});
            skArc(sketch, "E197.trimOffspring", {"start": v(6.19, -84.26) * mm, "mid": v(5.85, -83.61) * mm, "end": v(5.45, -83) * mm});
            skArc(sketch, "E198.trimOffspring", {"start": v(6.97, -86.9) * mm, "mid": v(6.84, -86.18) * mm, "end": v(6.66, -85.47) * mm});
            skArc(sketch, "E199.trimOffspring", {"start": v(6.9, -89.65) * mm, "mid": v(7, -88.93) * mm, "end": v(7.04, -88.2) * mm});
            skArc(sketch, "E200.trimOffspring", {"start": v(5.98, -92.25) * mm, "mid": v(6.3, -91.59) * mm, "end": v(6.57, -90.9) * mm});
            skArc(sketch, "E201.trimOffspring", {"start": v(4.3, -94.43) * mm, "mid": v(4.81, -93.9) * mm, "end": v(5.28, -93.34) * mm});
            skArc(sketch, "E202.trimOffspring", {"start": v(2.03, -95.99) * mm, "mid": v(2.68, -95.65) * mm, "end": v(3.3, -95.25) * mm});
            skArc(sketch, "E203.trimOffspring", {"start": v(-0.61, -96.77) * mm, "mid": v(0.11, -96.64) * mm, "end": v(0.82, -96.46) * mm});
            skArc(sketch, "E204.trimOffspring", {"start": v(-3.36, -96.7) * mm, "mid": v(-2.63, -96.8) * mm, "end": v(-1.9, -96.84) * mm});
            skArc(sketch, "E205.trimOffspring", {"start": v(-5.96, -95.77) * mm, "mid": v(-5.3, -96.1) * mm, "end": v(-4.61, -96.37) * mm});
            skArc(sketch, "E206.trimOffspring", {"start": v(-8.14, -94.1) * mm, "mid": v(-7.61, -94.6) * mm, "end": v(-7.04, -95.08) * mm});
            skSolve(sketch);
        }
        {
            var Q0;
            Q0=makeQuery(id+"F1.imprint","IMPRINT",FACE,{"disambiguationData":[TD([[makeQuery(id+"F1.imprint","IMPRINT",EDGE,{"derivedFrom":sQuery(id+"F1.wireOp",EDGE,"E111.21.1")}),-1.0]])]});
            extrude(context, id + "F2", {"entities" : qUnion([Q0]), "depth" : 3 * mm});
        }
        {
            var Q0;
            Q0=makeQuery(id+"F1.imprint","IMPRINT",FACE,{"disambiguationData":[TD([[makeQuery(id+"F1.imprint","IMPRINT",EDGE,{"derivedFrom":sQuery(id+"F1.wireOp",EDGE,"E112")}),-1.0]])]});
            extrude(context, id + "F3", {"entities" : qUnion([Q0]), "operationType" : NewBodyOperationType.ADD, "depth" : 5 * mm});
        }
        {
            var Q0;
            Q0=makeQuery(id+"F1.imprint","IMPRINT",FACE,{"disambiguationData":[TD([[makeQuery(id+"F1.imprint","IMPRINT",EDGE,{"derivedFrom":sQuery(id+"F1.wireOp",EDGE,"E133")}),-1.0]])]});
            var Q1;
            Q1=makeQuery(id+"F1.imprint","IMPRINT",FACE,{"disambiguationData":[TD([[makeQuery(id+"F1.imprint","IMPRINT",EDGE,{"derivedFrom":sQuery(id+"F1.wireOp",EDGE,"E154")}),-1.0]])]});
            var Q2;
            Q2=makeQuery(id+"F1.imprint","IMPRINT",FACE,{"disambiguationData":[TD([[makeQuery(id+"F1.imprint","IMPRINT",EDGE,{"derivedFrom":sQuery(id+"F1.wireOp",EDGE,"E155")}),-1.0]])]});
            var Q3;
            Q3=makeQuery(id+"F1.imprint","IMPRINT",FACE,{"disambiguationData":[TD([[makeQuery(id+"F1.imprint","IMPRINT",EDGE,{"derivedFrom":sQuery(id+"F1.wireOp",EDGE,"E160")}),-1.0]])]});
            var Q4;
            {var subQ0=sQuery(id+"F1.wireOp",EDGE,"E165");Q4=makeQuery(id+"F1.imprint","IMPRINT",FACE,{"disambiguationData":[TD([[makeQuery(id+"F1.imprint","IMPRINT",EDGE,{"derivedFrom":subQ0}),-1.0]])]});}
            var Q5;
            Q5=makeQuery(id+"F1.imprint","IMPRINT",FACE,{"disambiguationData":[TD([[makeQuery(id+"F1.imprint","IMPRINT",EDGE,{"derivedFrom":sQuery(id+"F1.wireOp",EDGE,"E159")}),-1.0]])]});
            var Q6;
            Q6=makeQuery(id+"F1.imprint","IMPRINT",FACE,{"disambiguationData":[TD([[makeQuery(id+"F1.imprint","IMPRINT",EDGE,{"derivedFrom":sQuery(id+"F1.wireOp",EDGE,"E153")}),-1.0]])]});
            var Q7;
            Q7=makeQuery(id+"F0.imprint","IMPRINT",FACE,{"disambiguationData":[TD([[makeQuery(id+"F0.imprint","IMPRINT",EDGE,{"derivedFrom":sQuery(id+"F0.wireOp",EDGE,"E16")}),1.0]])]});
            var Q8;
            {var subQ0=sQuery(id+"F0.wireOp",EDGE,"E30.11.0");Q8=makeQuery(id+"F0.imprint","IMPRINT",FACE,{"disambiguationData":[TD([[makeQuery(id+"F0.imprint","IMPRINT",EDGE,{"derivedFrom":subQ0}),-1.0]])]});}
            var Q9;
            {var subQ0=sQuery(id+"F0.wireOp",EDGE,"E30.10.0");Q9=makeQuery(id+"F0.imprint","IMPRINT",FACE,{"disambiguationData":[TD([[makeQuery(id+"F0.imprint","IMPRINT",EDGE,{"derivedFrom":subQ0}),-1.0]])]});}
            var Q10;
            {var subQ0=sQuery(id+"F0.wireOp",EDGE,"E30.16.0");Q10=makeQuery(id+"F0.imprint","IMPRINT",FACE,{"disambiguationData":[TD([[makeQuery(id+"F0.imprint","IMPRINT",EDGE,{"derivedFrom":subQ0}),-1.0]])]});}
            var Q11;
            {var subQ0=sQuery(id+"F0.wireOp",EDGE,"E30.13.0");Q11=makeQuery(id+"F0.imprint","IMPRINT",FACE,{"disambiguationData":[TD([[makeQuery(id+"F0.imprint","IMPRINT",EDGE,{"derivedFrom":subQ0}),-1.0]])]});}
            var Q12;
            {var subQ0=sQuery(id+"F0.wireOp",EDGE,"E30.17.0");Q12=makeQuery(id+"F0.imprint","IMPRINT",FACE,{"disambiguationData":[TD([[makeQuery(id+"F0.imprint","IMPRINT",EDGE,{"derivedFrom":subQ0}),-1.0]])]});}
            var Q13;
            {var subQ0=sQuery(id+"F0.wireOp",EDGE,"E30.14.0");Q13=makeQuery(id+"F0.imprint","IMPRINT",FACE,{"disambiguationData":[TD([[makeQuery(id+"F0.imprint","IMPRINT",EDGE,{"derivedFrom":subQ0}),-1.0]])]});}
            var Q14;
            {var subQ0=sQuery(id+"F0.wireOp",EDGE,"E30.18.0");Q14=makeQuery(id+"F0.imprint","IMPRINT",FACE,{"disambiguationData":[TD([[makeQuery(id+"F0.imprint","IMPRINT",EDGE,{"derivedFrom":subQ0}),-1.0]])]});}
            var Q15;
            {var subQ0=sQuery(id+"F0.wireOp",EDGE,"E30.15.0");Q15=makeQuery(id+"F0.imprint","IMPRINT",FACE,{"disambiguationData":[TD([[makeQuery(id+"F0.imprint","IMPRINT",EDGE,{"derivedFrom":subQ0}),-1.0]])]});}
            var Q16;
            Q16=makeQuery(id+"F0.imprint","IMPRINT",FACE,{"disambiguationData":[TD([[makeQuery(id+"F0.imprint","IMPRINT",EDGE,{"derivedFrom":sQuery(id+"F0.wireOp",EDGE,"E16")}),-1.0]])]});
            var Q17;
            {var subQ0=sQuery(id+"F0.wireOp",EDGE,"E30.3.0");Q17=makeQuery(id+"F0.imprint","IMPRINT",FACE,{"disambiguationData":[TD([[makeQuery(id+"F0.imprint","IMPRINT",EDGE,{"derivedFrom":subQ0}),-1.0]])]});}
            var Q18;
            {var subQ0=sQuery(id+"F0.wireOp",EDGE,"E30.4.0");Q18=makeQuery(id+"F0.imprint","IMPRINT",FACE,{"disambiguationData":[TD([[makeQuery(id+"F0.imprint","IMPRINT",EDGE,{"derivedFrom":subQ0}),-1.0]])]});}
            var Q19;
            {var subQ0=sQuery(id+"F0.wireOp",EDGE,"E30.5.0");Q19=makeQuery(id+"F0.imprint","IMPRINT",FACE,{"disambiguationData":[TD([[makeQuery(id+"F0.imprint","IMPRINT",EDGE,{"derivedFrom":subQ0}),-1.0]])]});}
            var Q20;
            {var subQ0=sQuery(id+"F0.wireOp",EDGE,"E30.6.0");Q20=makeQuery(id+"F0.imprint","IMPRINT",FACE,{"disambiguationData":[TD([[makeQuery(id+"F0.imprint","IMPRINT",EDGE,{"derivedFrom":subQ0}),-1.0]])]});}
            var Q21;
            {var subQ0=sQuery(id+"F0.wireOp",EDGE,"E30.7.0");Q21=makeQuery(id+"F0.imprint","IMPRINT",FACE,{"disambiguationData":[TD([[makeQuery(id+"F0.imprint","IMPRINT",EDGE,{"derivedFrom":subQ0}),-1.0]])]});}
            var Q22;
            {var subQ0=sQuery(id+"F0.wireOp",EDGE,"E30.8.0");Q22=makeQuery(id+"F0.imprint","IMPRINT",FACE,{"disambiguationData":[TD([[makeQuery(id+"F0.imprint","IMPRINT",EDGE,{"derivedFrom":subQ0}),-1.0]])]});}
            var Q23;
            {var subQ0=sQuery(id+"F0.wireOp",EDGE,"E30.9.0");Q23=makeQuery(id+"F0.imprint","IMPRINT",FACE,{"disambiguationData":[TD([[makeQuery(id+"F0.imprint","IMPRINT",EDGE,{"derivedFrom":subQ0}),-1.0]])]});}
            var Q24;
            {var subQ0=sQuery(id+"F0.wireOp",EDGE,"E30.12.0");Q24=makeQuery(id+"F0.imprint","IMPRINT",FACE,{"disambiguationData":[TD([[makeQuery(id+"F0.imprint","IMPRINT",EDGE,{"derivedFrom":subQ0}),-1.0]])]});}
            var Q25;
            {var subQ0=sQuery(id+"F0.wireOp",EDGE,"E30.19.0");Q25=makeQuery(id+"F0.imprint","IMPRINT",FACE,{"disambiguationData":[TD([[makeQuery(id+"F0.imprint","IMPRINT",EDGE,{"derivedFrom":subQ0}),-1.0]])]});}
            var Q26;
            {var subQ0=sQuery(id+"F0.wireOp",EDGE,"E27");Q26=makeQuery(id+"F0.imprint","IMPRINT",FACE,{"disambiguationData":[TD([[makeQuery(id+"F0.imprint","IMPRINT",EDGE,{"derivedFrom":subQ0}),-1.0]])]});}
            var Q27;
            {var subQ0=sQuery(id+"F0.wireOp",EDGE,"E30.1.0");Q27=makeQuery(id+"F0.imprint","IMPRINT",FACE,{"disambiguationData":[TD([[makeQuery(id+"F0.imprint","IMPRINT",EDGE,{"derivedFrom":subQ0}),-1.0]])]});}
            var Q28;
            {var subQ0=sQuery(id+"F0.wireOp",EDGE,"E30.2.0");Q28=makeQuery(id+"F0.imprint","IMPRINT",FACE,{"disambiguationData":[TD([[makeQuery(id+"F0.imprint","IMPRINT",EDGE,{"derivedFrom":subQ0}),-1.0]])]});}
            extrude(context, id + "F4", {"entities" : qUnion([Q0, Q1, Q2, Q3, Q4, Q5, Q6, Q7, Q8, Q9, Q10, Q11, Q12, Q13, Q14, Q15, Q16, Q17, Q18, Q19, Q20, Q21, Q22, Q23, Q24, Q25, Q26, Q27, Q28]), "depth" : 3 * mm});
        }
        {
            var Q0;
            Q0=makeQuery(id+"F0.imprint","IMPRINT",FACE,{"disambiguationData":[TD([[makeQuery(id+"F0.imprint","IMPRINT",EDGE,{"derivedFrom":sQuery(id+"F0.wireOp",EDGE,"E31")}),-1.0]])]});
            extrude(context, id + "F5", {"entities" : qUnion([Q0]), "depth" : 8 * mm});
        }
        {
            var Q0;
            Q0=makeQuery(id+"F0.imprint","IMPRINT",FACE,{"disambiguationData":[TD([[makeQuery(id+"F0.imprint","IMPRINT",EDGE,{"derivedFrom":sQuery(id+"F0.wireOp",EDGE,"E35")}),1.0]])]});
            extrude(context, id + "F6", {"entities" : qUnion([Q0]), "operationType" : NewBodyOperationType.ADD, "depth" : 3 * mm});
        }
        {
            var Q0;
            Q0=makeQuery(id+"F0.imprint","IMPRINT",FACE,{"disambiguationData":[TD([[makeQuery(id+"F0.imprint","IMPRINT",EDGE,{"derivedFrom":sQuery(id+"F0.wireOp",EDGE,"E16")}),1.0]])]});
            extrude(context, id + "F7", {"entities" : qUnion([Q0]), "operationType" : NewBodyOperationType.REMOVE, "depth" : 25 * mm});
        }
        {
            var Q0;
            Q0=qCreatedBy(makeId("Front.planeOp"),FACE);
            var sketch = newSketch(context, id + "F8", { "sketchPlane" : qUnion([Q0])});
            skLineSegment(sketch, "E207.bottom", {"start": v(32.18, 73.41) * mm, "end": v(92.18, 73.41) * mm});
            skLineSegment(sketch, "E208.top", {"start": v(32.18, 65.41) * mm, "end": v(84.18, 65.41) * mm, "construction": true});
            skLineSegment(sketch, "E207.top", {"start": v(32.18, 13.41) * mm, "end": v(92.18, 13.41) * mm});
            skLineSegment(sketch, "E209", {"start": v(40.18, 43.41) * mm, "end": v(70.18, 43.41) * mm, "construction": true});
            skLineSegment(sketch, "E207.left", {"start": v(32.18, 73.41) * mm, "end": v(32.18, 13.41) * mm});
            skLineSegment(sketch, "E210.1.0.0", {"start": v(148.26, 73.41) * mm, "end": v(148.26, 43.41) * mm, "construction": true});
            skLineSegment(sketch, "E207.right", {"start": v(92.18, 73.41) * mm, "end": v(92.18, 13.41) * mm});
            skLineSegment(sketch, "E210.1.0.1", {"start": v(148.26, 43.41) * mm, "end": v(178.26, 43.41) * mm, "construction": true});
            skLineSegment(sketch, "E210.1.0.2", {"start": v(140.26, 73.41) * mm, "end": v(200.26, 73.41) * mm});
            skLineSegment(sketch, "E210.1.0.3", {"start": v(200.26, 73.41) * mm, "end": v(200.26, 13.41) * mm});
            skLineSegment(sketch, "E211.right", {"start": v(40.18, 73.41) * mm, "end": v(40.18, 43.41) * mm, "construction": true});
            skLineSegment(sketch, "E210.1.0.5", {"start": v(148.26, 43.41) * mm, "end": v(192.26, 65.41) * mm, "construction": true});
            skLineSegment(sketch, "E212.0", {"start": v(-78.13, 67.64) * mm, "end": v(-35.8, 67.64) * mm});
            skLineSegment(sketch, "E212.1", {"start": v(-120.48, 67.64) * mm, "end": v(-78.13, 67.64) * mm});
            skLineSegment(sketch, "E210.1.0.8", {"start": v(140.26, 73.41) * mm, "end": v(140.26, 13.41) * mm});
            skLineSegment(sketch, "E213.1", {"start": v(-113.66, 63.14) * mm, "end": v(-78.13, 63.14) * mm});
            skLineSegment(sketch, "E210.1.0.9", {"start": v(140.26, 13.41) * mm, "end": v(200.26, 13.41) * mm});
            skLineSegment(sketch, "E213.2", {"start": v(-78.13, 63.14) * mm, "end": v(-42.6, 63.14) * mm});
            skLineSegment(sketch, "E214", {"start": v(40.18, 43.41) * mm, "end": v(84.18, 65.41) * mm, "construction": true});
            skLineSegment(sketch, "E210.1.0.10", {"start": v(140.26, 65.41) * mm, "end": v(192.26, 65.41) * mm, "construction": true});
            skLineSegment(sketch, "E215.trimOffspring", {"start": v(-76.21, 45.44) * mm, "end": v(-42.6, 63.14) * mm});
            skLineSegment(sketch, "E216.trimOffspring", {"start": v(-75.14, 42.96) * mm, "end": v(-35.79, 62.64) * mm});
            skLineSegment(sketch, "E210.1.0.14", {"start": v(140.26, 73.41) * mm, "end": v(192.26, 73.41) * mm, "construction": true});
            skLineSegment(sketch, "E217", {"start": v(-78.13, 43.14) * mm, "end": v(-34.13, 65.14) * mm, "construction": true});
            skLineSegment(sketch, "E211.left", {"start": v(32.18, 73.41) * mm, "end": v(32.18, 43.41) * mm, "construction": true});
            skLineSegment(sketch, "E218", {"start": v(148.26, 43.41) * mm, "end": v(163.26, 30.18) * mm, "construction": true});
            skLineSegment(sketch, "E219.1", {"start": v(-121.77, 62.16) * mm, "end": v(-80.73, 41.64) * mm});
            skLineSegment(sketch, "E213.0", {"start": v(-113.66, 63.14) * mm, "end": v(-79.24, 45.93) * mm});
            skLineSegment(sketch, "E220", {"start": v(-122.13, 65.14) * mm, "end": v(-78.13, 65.14) * mm, "construction": true});
            skLineSegment(sketch, "E221", {"start": v(-78.13, 65.14) * mm, "end": v(-34.13, 65.14) * mm, "construction": true});
            skLineSegment(sketch, "E210.1.0.12", {"start": v(140.26, 73.41) * mm, "end": v(140.26, 43.41) * mm, "construction": true});
            skLineSegment(sketch, "E208.bottom", {"start": v(32.18, 73.41) * mm, "end": v(84.18, 73.41) * mm, "construction": true});
            skLineSegment(sketch, "E210.1.0.13", {"start": v(140.26, 73.41) * mm, "end": v(192.26, 73.41) * mm, "construction": true});
            skLineSegment(sketch, "E222", {"start": v(-78.13, 65.14) * mm, "end": v(-78.13, 43.14) * mm, "construction": true});
            skLineSegment(sketch, "E223", {"start": v(-122.13, 65.14) * mm, "end": v(-78.13, 43.14) * mm, "construction": true});
            skCircle(sketch, "E224", {"center": v(70.18, 43.41) * mm, "radius": 1.5 * mm});
            skLineSegment(sketch, "E225.left", {"start": v(32.18, 73.41) * mm, "end": v(32.18, 58.41) * mm, "construction": true});
            skLineSegment(sketch, "E210.1.0.15", {"start": v(140.26, 73.41) * mm, "end": v(140.26, 58.41) * mm, "construction": true});
            skLineSegment(sketch, "E226", {"start": v(163.26, 30.18) * mm, "end": v(178.26, 43.41) * mm, "construction": true});
            skCircle(sketch, "E227", {"center": v(163.26, 30.18) * mm, "radius": 1.5 * mm});
            skCircle(sketch, "E210.1.0.7", {"center": v(178.26, 43.41) * mm, "radius": 1.5 * mm});
            skLineSegment(sketch, "E210.1.0.16", {"start": v(192.26, 73.41) * mm, "end": v(192.26, 65.41) * mm, "construction": true});
            skLineSegment(sketch, "E208.right", {"start": v(84.18, 73.41) * mm, "end": v(84.18, 65.41) * mm, "construction": true});
            skCircle(sketch, "E228", {"center": v(84.18, 65.41) * mm, "radius": 1.5 * mm});
            skCircle(sketch, "E210.1.0.6", {"center": v(192.26, 65.41) * mm, "radius": 1.5 * mm});
            skCircle(sketch, "E229", {"center": v(-122.13, 65.14) * mm, "radius": 1.5 * mm});
            skCircle(sketch, "E230", {"center": v(-34.13, 65.14) * mm, "radius": 1.5 * mm});
            skLineSegment(sketch, "E211.top", {"start": v(32.18, 43.41) * mm, "end": v(40.18, 43.41) * mm, "construction": true});
            skArc(sketch, "E231", {"start": v(-120.48, 67.64) * mm, "mid": v(-125.05, 65.83) * mm, "end": v(-121.77, 62.16) * mm});
            skArc(sketch, "E232", {"start": v(-35.79, 62.64) * mm, "mid": v(-31.13, 65.14) * mm, "end": v(-35.8, 67.64) * mm});
            skCircle(sketch, "E233", {"center": v(40.18, 43.41) * mm, "radius": 1.5 * mm});
            skArc(sketch, "E234.trimOffspring", {"start": v(-76.21, 45.44) * mm, "mid": v(-77.66, 46.1) * mm, "end": v(-79.24, 45.93) * mm});
            skCircle(sketch, "E210.1.0.18", {"center": v(148.26, 43.41) * mm, "radius": 1.5 * mm});
            skCircle(sketch, "E235", {"center": v(-78.13, 43.14) * mm, "radius": 1.5 * mm});
            skArc(sketch, "E236", {"start": v(-80.73, 41.64) * mm, "mid": v(-77.45, 40.22) * mm, "end": v(-75.14, 42.96) * mm});
            skLineSegment(sketch, "E210.1.0.4", {"start": v(140.26, 43.41) * mm, "end": v(148.26, 43.41) * mm, "construction": true});
            skLineSegment(sketch, "E208.left", {"start": v(32.18, 73.41) * mm, "end": v(32.18, 65.41) * mm, "construction": true});
            skLineSegment(sketch, "E211.bottom", {"start": v(32.18, 73.41) * mm, "end": v(40.18, 73.41) * mm, "construction": true});
            skLineSegment(sketch, "E210.1.0.17", {"start": v(140.26, 73.41) * mm, "end": v(140.26, 65.41) * mm, "construction": true});
            skLineSegment(sketch, "E210.1.0.11", {"start": v(140.26, 73.41) * mm, "end": v(148.26, 73.41) * mm, "construction": true});
            skLineSegment(sketch, "E237.right", {"start": v(-161.27, 71.44) * mm, "end": v(-161.27, 41.44) * mm, "construction": true});
            skLineSegment(sketch, "E238.top", {"start": v(-153.27, 63.44) * mm, "end": v(-205.27, 63.44) * mm, "construction": true});
            skLineSegment(sketch, "E239.bottom", {"start": v(-153.27, 24.67) * mm, "end": v(-291.85, 24.67) * mm});
            skLineSegment(sketch, "E240.trimOffspring", {"start": v(-213.27, 41.51) * mm, "end": v(-291.85, 41.51) * mm});
            skLineSegment(sketch, "E241", {"start": v(-205.27, 63.44) * mm, "end": v(-161.27, 41.44) * mm, "construction": true});
            skLineSegment(sketch, "E242.top", {"start": v(-153.27, 71.44) * mm, "end": v(-213.27, 71.44) * mm});
            skLineSegment(sketch, "E242.left", {"start": v(-153.27, 44.39) * mm, "end": v(-153.27, 71.44) * mm});
            skLineSegment(sketch, "E242.right", {"start": v(-213.27, 41.51) * mm, "end": v(-213.27, 71.44) * mm});
            skLineSegment(sketch, "E237.left", {"start": v(-153.27, 71.44) * mm, "end": v(-153.27, 41.44) * mm, "construction": true});
            skLineSegment(sketch, "E238.bottom", {"start": v(-153.27, 71.44) * mm, "end": v(-205.27, 71.44) * mm, "construction": true});
            skLineSegment(sketch, "E239.left", {"start": v(-153.27, 24.67) * mm, "end": v(-153.27, 44.39) * mm});
            skLineSegment(sketch, "E239.right", {"start": v(-291.85, 24.67) * mm, "end": v(-291.85, 41.51) * mm});
            skCircle(sketch, "E243", {"center": v(-161.27, 41.44) * mm, "radius": 1.5 * mm});
            skCircle(sketch, "E244", {"center": v(-205.27, 63.44) * mm, "radius": 1.5 * mm});
            skLineSegment(sketch, "E238.right", {"start": v(-205.27, 71.44) * mm, "end": v(-205.27, 63.44) * mm, "construction": true});
            skLineSegment(sketch, "E237.bottom", {"start": v(-153.27, 71.44) * mm, "end": v(-161.27, 71.44) * mm, "construction": true});
            skLineSegment(sketch, "E238.left", {"start": v(-153.27, 71.44) * mm, "end": v(-153.27, 63.44) * mm, "construction": true});
            skSolve(sketch);
        }
        {
            var Q0;
            Q0=makeQuery(id+"F8.imprint","IMPRINT",FACE,{"disambiguationData":[TD([[makeQuery(id+"F8.imprint","IMPRINT",EDGE,{"derivedFrom":sQuery(id+"F8.wireOp",EDGE,"E210.1.0.2")}),-1.0]])]});
            var Q1;
            Q1=makeQuery(id+"F8.imprint","IMPRINT",FACE,{"disambiguationData":[TD([[makeQuery(id+"F8.imprint","IMPRINT",EDGE,{"derivedFrom":sQuery(id+"F8.wireOp",EDGE,"E239.bottom")}),-1.0]])]});
            var Q2;
            Q2=makeQuery(id+"F8.imprint","IMPRINT",FACE,{"disambiguationData":[TD([[makeQuery(id+"F8.imprint","IMPRINT",EDGE,{"derivedFrom":sQuery(id+"F8.wireOp",EDGE,"E212.0")}),-1.0]])]});
            extrude(context, id + "F9", {"entities" : qUnion([Q0, Q1, Q2]), "depth" : 4 * mm});
        }
    });
